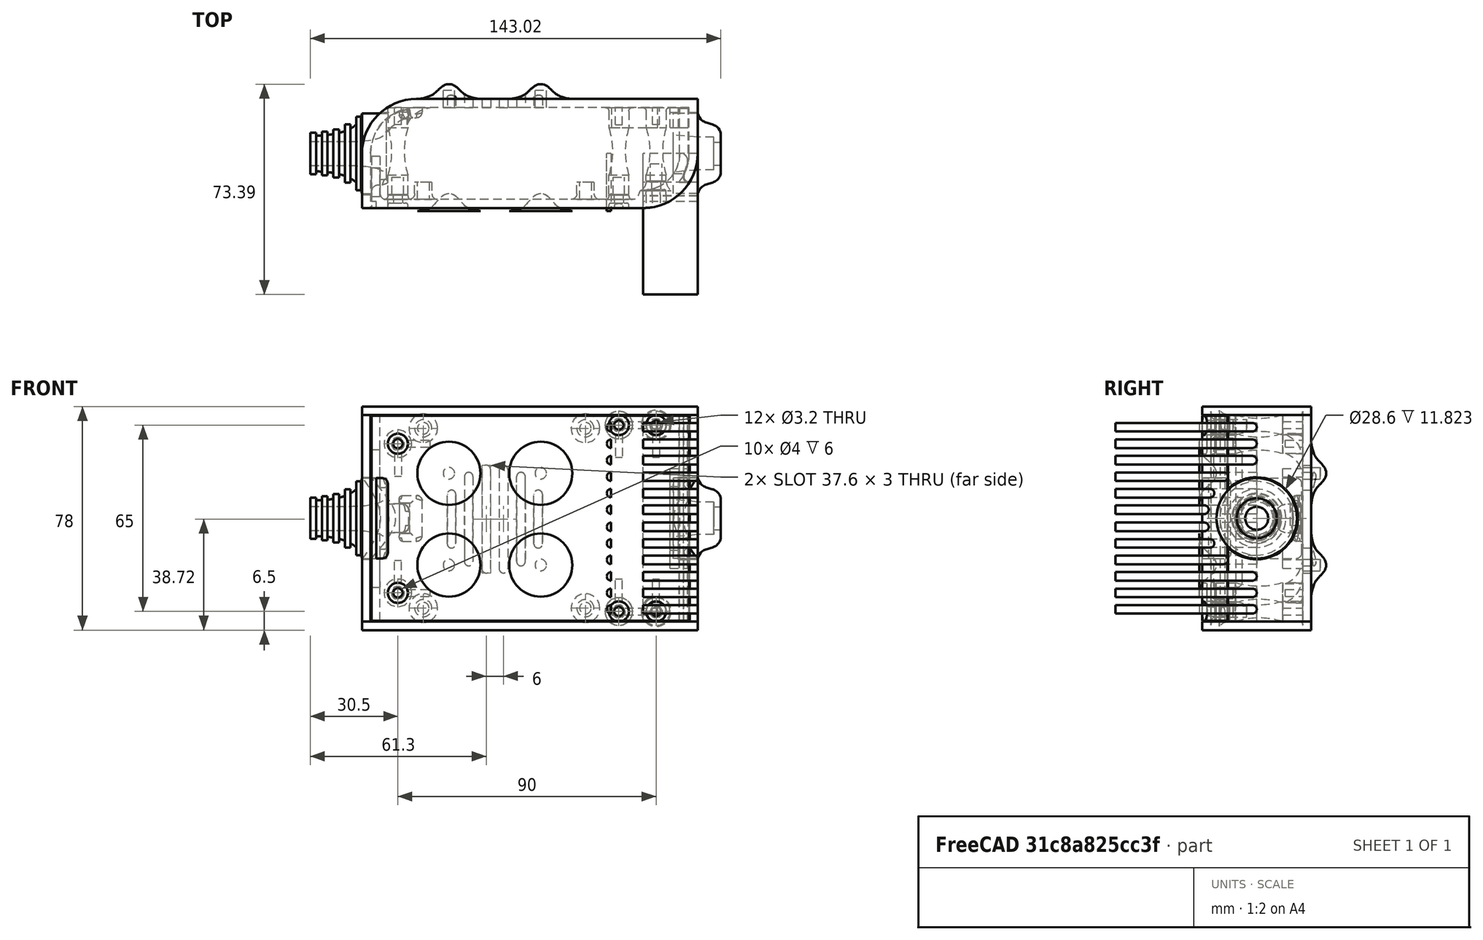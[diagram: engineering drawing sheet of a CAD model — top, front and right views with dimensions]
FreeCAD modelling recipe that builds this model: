
FCSTD DOCUMENT  (FreeCAD 0.19R0.19.2)
Label: enclosure_112
License: All rights reserved
LicenseURL: http://en.wikipedia.org/wiki/All_rights_reserved
objects: Part::Feature×72, Part::Revolution×72, Part::MultiFuse×53, Sketcher::SketchObject×31, Part::Fillet×22, Part::Cylinder×22, Part::Extrusion×21, Part::Cut×20, Part::Box×12, App::MeasureDistance×4
note: 325 computed .brp shape members not serialized (recipe doc carries the construction recipe); baked Part::Feature solids carry a one-line shape summary decoded from their .brp

FEATURE [Sketcher::SketchObject] Sketch  label="topSketch"
  FullyConstrained = true
  sketch-geometry (13):
    g0: LineSegment StartX=117 StartY=19 StartZ=0 EndX=117 EndY=38 EndZ=0
    g1: ArcOfCircle CenterX=98 CenterY=19 CenterZ=0 NormalX=0 NormalY=0 NormalZ=1 AngleXU=0 Radius=19 StartAngle=5.7297 EndAngle=6.28319
    g2: LineSegment StartX=0 StartY=3 StartZ=0 EndX=0 EndY=19 EndZ=0
    g3: LineSegment StartX=19 StartY=38 StartZ=0 EndX=117 EndY=38 EndZ=0
    g4: ArcOfCircle CenterX=19 CenterY=19 CenterZ=0 NormalX=0 NormalY=0 NormalZ=1 AngleXU=0 Radius=19 StartAngle=1.5708 EndAngle=3.14159
    g5: ArcOfCircle CenterX=19 CenterY=19 CenterZ=0 NormalX=0 NormalY=0 NormalZ=1 AngleXU=0 Radius=16 StartAngle=1.5708 EndAngle=3.14159
    g6: ArcOfCircle CenterX=98 CenterY=19 CenterZ=0 NormalX=0 NormalY=0 NormalZ=1 AngleXU=0 Radius=16 StartAngle=5.60905 EndAngle=6.28319
    g7: LineSegment StartX=114 StartY=19 StartZ=0 EndX=114 EndY=35 EndZ=0
    g8: LineSegment StartX=110.5 StartY=9.01251 StartZ=0 EndX=114.163 EndY=9.01251 EndZ=0
    g9: LineSegment StartX=114 StartY=35 StartZ=0 EndX=19 EndY=35 EndZ=0
    g10: LineSegment StartX=0 StartY=3 StartZ=0 EndX=0 EndY=0 EndZ=0
    g11: LineSegment StartX=3 StartY=0 StartZ=0 EndX=0 EndY=0 EndZ=0
    g12: LineSegment StartX=3 StartY=19 StartZ=0 EndX=3 EndY=0 EndZ=0
  constraints (33):
    c: Vertical(g0)
    c: Distance(g0) = 19
    c: Block(g0)
    c: Coincident(g1,g0)
    c: Block(g1)
    c: Vertical(g2)
    c: Block(g2)
    c: Coincident(g3,g0)
    c: Horizontal(g3)
    c: Distance(g3) = 98
    c: Coincident(g4,g3)
    c: Coincident(g4,g2)
    c: Block(g4)
    c: Coincident(g5,g4)
    c: Coincident(g6,g1)
    c: Block(g6)
    c: Block(g5)
    c: Coincident(g7,g6)
    c: Vertical(g7)
    c: Coincident(g8,g6)
    c: Coincident(g8,g1)
    c: Coincident(g9,g7)
    c: Coincident(g9,g5)
    c: Horizontal(g9)
    c: Tangent(g9,g5)
    c: Coincident(g10,g2)
    c: Distance(g10) = 3
    c: Vertical(g10)
    c: Coincident(g11,g10)
    c: Horizontal(g11)
    c: Coincident(g12,g5)
    c: Coincident(g12,g11)
    c: Vertical(g12)
FEATURE [Sketcher::SketchObject] Sketch001  label="bottomSketch"
  FullyConstrained = true
  sketch-geometry (32):
    g0: LineSegment StartX=3.3 StartY=-6.03275e-07 StartZ=0 EndX=98 EndY=-6.03275e-07 EndZ=0
    g1: ArcOfCircle CenterX=98 CenterY=19 CenterZ=0 NormalX=0 NormalY=0 NormalZ=1 AngleXU=0 Radius=19 StartAngle=4.71239 EndAngle=5.71103
    g2: LineSegment StartX=6.3 StartY=8 StartZ=0 EndX=3.3 EndY=8 EndZ=0
    g3: LineSegment StartX=3.3 StartY=8 StartZ=0 EndX=3.3 EndY=-6.03275e-07 EndZ=0
    g4: ArcOfCircle CenterX=8.3 CenterY=5 CenterZ=0 NormalX=0 NormalY=0 NormalZ=1 AngleXU=0 Radius=2 StartAngle=3.14159 EndAngle=4.71239
    g5: LineSegment StartX=6.3 StartY=8 StartZ=0 EndX=6.3 EndY=5 EndZ=0
    g6: ArcOfCircle CenterX=98 CenterY=19 CenterZ=0 NormalX=0 NormalY=0 NormalZ=1 AngleXU=0 Radius=12.7 StartAngle=4.71239 EndAngle=6.28319
    g7: LineSegment StartX=94.7 StartY=3 StartZ=0 EndX=8.3 EndY=3 EndZ=0
    g8-g12: Circle x5 (B-spline internal-alignment scaffolding for g13; pole/knot coordinates omitted)
    g13: BSplineCurve PolesCount=5 KnotsCount=3 Degree=3 IsPeriodic=0
    g14: GeomPoint X=98 Y=6.3 Z=0
    g15: GeomPoint X=96.3938 Y=4.71946 Z=0
    g16: GeomPoint X=94.7 Y=3 Z=0
    g17-g23: Circle x7 (B-spline internal-alignment scaffolding for g24; pole/knot coordinates omitted)
    g24: BSplineCurve PolesCount=7 KnotsCount=5 Degree=3 IsPeriodic=0
    g25-g29: GeomPoint x5 (B-spline internal-alignment scaffolding for g24; pole/knot coordinates omitted)
    g30: ArcOfCircle CenterX=98 CenterY=19 CenterZ=0 NormalX=0 NormalY=0 NormalZ=1 AngleXU=0 Radius=15.7 StartAngle=5.81226 EndAngle=6.28319
    g31: LineSegment StartX=110.7 StartY=19 StartZ=0 EndX=113.7 EndY=19 EndZ=0
  constraints (41):
    c: Horizontal(g0)
    c: Coincident(g1,g0)
    c: Block(g1)
    c: Horizontal(g2)
    c: Distance(g2) = 3
    c: Coincident(g3,g2)
    c: Vertical(g3)
    c: Coincident(g3,g0)
    c: Block(g4)
    c: Block(g2)
    c: Coincident(g5,g2)
    c: Coincident(g5,g4)
    c: Vertical(g5)
    c: Coincident(g6,g1)
    c: Block(g6)
    c: Coincident(g7,g4)
    c: Horizontal(g7)
    c: Block(g0)
    c: Block(g7)
    c: Block(g3)
    c: Coincident(g13,g6)
    c: Weight(g8) = 1
    c: Equal(g8, g9-g12) x4
    c: Coincident(g13,g7)
    c: InternalAlignment(g8-g12 -> g13) x5
    c: InternalAlignment(g14,g13)
    c: InternalAlignment(g15,g13)
    c: InternalAlignment(g16,g13)
    c: Block(g13)
    c: Weight(g17) = 1
    c: Equal(g17, g18-g23) x6
    c: Coincident(g24,g1)
    c: InternalAlignment(g17-g23 -> g24) x7
    c: InternalAlignment(g25-g29 -> g24) x5
    c: Block(g24)
    c: Coincident(g30,g24)
    c: Coincident(g31,g6)
    c: Coincident(g31,g30)
    c: Horizontal(g31)
    c: Block(g31)
    c: Block(g30)
FEATURE [Part::Extrusion] Extrude  label="top"
  Base = -> Sketch
  Dir = (0,0,1)
  DirMode = 2
  FaceMakerClass = Part::FaceMakerBullseye
  LengthFwd = 72
  LengthRev = 0
  Solid = true
  Symmetric = false
FEATURE [Part::Extrusion] Extrude001  label="bottom"
  Base = -> Sketch001
  Dir = (0,0,1)
  DirMode = 2
  FaceMakerClass = Part::FaceMakerBullseye
  LengthFwd = 71.4
  LengthRev = 0
  Placement = pos=(0,0,0.3) rot=(0,0,1;0rad)
  Solid = true
  Symmetric = false
FEATURE [Sketcher::SketchObject] Sketch002  label="topSketch001"
  FullyConstrained = true
  sketch-geometry (6):
    g0: LineSegment StartX=19 StartY=38 StartZ=0 EndX=117 EndY=38 EndZ=0
    g1: ArcOfCircle CenterX=19 CenterY=19 CenterZ=0 NormalX=0 NormalY=0 NormalZ=1 AngleXU=0 Radius=19 StartAngle=1.5708 EndAngle=3.14159
    g2: LineSegment StartX=117 StartY=38 StartZ=0 EndX=117 EndY=19 EndZ=0
    g3: LineSegment StartX=98 StartY=1.0161e-12 StartZ=0 EndX=5.22862e-06 EndY=1.0161e-12 EndZ=0
    g4: LineSegment StartX=5.22862e-06 StartY=19 StartZ=0 EndX=5.22862e-06 EndY=1.0161e-12 EndZ=0
    g5: ArcOfCircle CenterX=98 CenterY=19 CenterZ=0 NormalX=0 NormalY=0 NormalZ=1 AngleXU=0 Radius=19 StartAngle=4.71239 EndAngle=6.28319
  constraints (16):
    c: Horizontal(g0)
    c: Distance(g0) = 98
    c: Coincident(g1,g0)
    c: Block(g1)
    c: Coincident(g2,g0)
    c: Vertical(g2)
    c: Distance(g2) = 19
    c: Horizontal(g3)
    c: Coincident(g4,g1)
    c: Vertical(g4)
    c: Coincident(g3,g4)
    c: Block(g3)
    c: Coincident(g5,g2)
    c: Coincident(g5,g3)
    c: Block(g0)
    c: Block(g5)
FEATURE [Part::Extrusion] Extrude002  label="sideA"
  Base = -> Sketch002
  Dir = (0,0,1)
  DirMode = 2
  FaceMakerClass = Part::FaceMakerBullseye
  LengthFwd = 3
  LengthRev = 0
  Placement = pos=(0,0,-3) rot=(0,0,1;0rad)
  Solid = true
  Symmetric = false
FEATURE [Sketcher::SketchObject] Sketch003  label="topSketch002"
  FullyConstrained = true
  sketch-geometry (6):
    g0: LineSegment StartX=19 StartY=38 StartZ=0 EndX=117 EndY=38 EndZ=0
    g1: ArcOfCircle CenterX=19 CenterY=19 CenterZ=0 NormalX=0 NormalY=0 NormalZ=1 AngleXU=0 Radius=19 StartAngle=1.5708 EndAngle=3.14159
    g2: LineSegment StartX=117 StartY=38 StartZ=0 EndX=117 EndY=19 EndZ=0
    g3: LineSegment StartX=98 StartY=1.0161e-12 StartZ=0 EndX=5.22862e-06 EndY=1.0161e-12 EndZ=0
    g4: LineSegment StartX=5.22862e-06 StartY=19 StartZ=0 EndX=5.22862e-06 EndY=1.0161e-12 EndZ=0
    g5: ArcOfCircle CenterX=98 CenterY=19 CenterZ=0 NormalX=0 NormalY=0 NormalZ=1 AngleXU=0 Radius=19 StartAngle=4.71239 EndAngle=6.28319
  constraints (16):
    c: Horizontal(g0)
    c: Distance(g0) = 98
    c: Coincident(g1,g0)
    c: Block(g1)
    c: Coincident(g2,g0)
    c: Vertical(g2)
    c: Distance(g2) = 19
    c: Horizontal(g3)
    c: Coincident(g4,g1)
    c: Vertical(g4)
    c: Coincident(g3,g4)
    c: Block(g3)
    c: Coincident(g5,g2)
    c: Coincident(g5,g3)
    c: Block(g0)
    c: Block(g5)
FEATURE [Part::Extrusion] Extrude003  label="sideB"
  Base = -> Sketch003
  Dir = (0,0,1)
  DirMode = 2
  FaceMakerClass = Part::FaceMakerBullseye
  LengthFwd = 3
  LengthRev = 0
  Placement = pos=(0,0,72) rot=(0,0,1;0rad)
  Solid = true
  Symmetric = false
FEATURE [Sketcher::SketchObject] Sketch004
  FullyConstrained = true
  MapMode = 3
  Placement = pos=(0,0,0) rot=(1,0,0;1.5708rad)
  Support = -> [Extrude]
  sketch-geometry (8):
    g0: Circle CenterX=80.351 CenterY=-67.6202 CenterZ=0 NormalX=0 NormalY=0 NormalZ=1 AngleXU=0 Radius=2
    g1: Circle CenterX=80.351 CenterY=-67.6202 CenterZ=0 NormalX=0 NormalY=0 NormalZ=1 AngleXU=0 Radius=3
    g2: Circle CenterX=80.351 CenterY=-4.92017 CenterZ=0 NormalX=0 NormalY=0 NormalZ=1 AngleXU=0 Radius=2
    g3: Circle CenterX=80.351 CenterY=-4.92017 CenterZ=0 NormalX=0 NormalY=0 NormalZ=1 AngleXU=0 Radius=3
    g4: Circle CenterX=23.851 CenterY=-4.92017 CenterZ=0 NormalX=0 NormalY=0 NormalZ=1 AngleXU=0 Radius=2
    g5: Circle CenterX=23.851 CenterY=-4.92017 CenterZ=0 NormalX=0 NormalY=0 NormalZ=1 AngleXU=0 Radius=3
    g6: Circle CenterX=23.851 CenterY=-67.6202 CenterZ=0 NormalX=0 NormalY=0 NormalZ=1 AngleXU=0 Radius=2
    g7: Circle CenterX=23.851 CenterY=-67.6202 CenterZ=0 NormalX=0 NormalY=0 NormalZ=1 AngleXU=0 Radius=3
  constraints (8):
    c: Block(g3)
    c: Block(g2)
    c: Block(g1)
    c: Block(g0)
    c: Block(g6)
    c: Block(g7)
    c: Block(g4)
    c: Block(g5)
FEATURE [Part::Extrusion] Extrude004
  Base = -> Sketch004
  Dir = (0,-1,2e-16)
  DirMode = 2
  FaceMakerClass = Part::FaceMakerBullseye
  LengthFwd = 6
  LengthRev = 0
  Placement = pos=(0,9,0) rot=(0,0,1;0rad)
  Solid = true
  Symmetric = false
FEATURE [Sketcher::SketchObject] Sketch005
  FullyConstrained = true
  MapMode = 3
  Placement = pos=(0,0,0) rot=(1,0,0;1.5708rad)
  Support = -> [Extrude]
  sketch-geometry (8):
    g0: Circle CenterX=80.351 CenterY=-67.6202 CenterZ=0 NormalX=0 NormalY=0 NormalZ=1 AngleXU=0 Radius=3
    g1: Circle CenterX=80.351 CenterY=-4.92017 CenterZ=0 NormalX=0 NormalY=0 NormalZ=1 AngleXU=0 Radius=3
    g2: Circle CenterX=23.851 CenterY=-4.92017 CenterZ=0 NormalX=0 NormalY=0 NormalZ=1 AngleXU=0 Radius=3
    g3: Circle CenterX=23.851 CenterY=-67.6202 CenterZ=0 NormalX=0 NormalY=0 NormalZ=1 AngleXU=0 Radius=3
    g4: Circle CenterX=23.851 CenterY=-67.6202 CenterZ=0 NormalX=0 NormalY=0 NormalZ=1 AngleXU=0 Radius=5
    g5: Circle CenterX=80.351 CenterY=-67.6202 CenterZ=0 NormalX=0 NormalY=0 NormalZ=1 AngleXU=0 Radius=5
    g6: Circle CenterX=23.851 CenterY=-4.92017 CenterZ=0 NormalX=0 NormalY=0 NormalZ=1 AngleXU=0 Radius=5
    g7: Circle CenterX=80.351 CenterY=-4.92017 CenterZ=0 NormalX=0 NormalY=0 NormalZ=1 AngleXU=0 Radius=5
  constraints (8):
    c: Block(g1)
    c: Block(g0)
    c: Block(g3)
    c: Block(g2)
    c: Block(g5)
    c: Block(g4)
    c: Block(g6)
    c: Block(g7)
FEATURE [Part::Extrusion] Extrude005
  Base = -> Sketch005
  Dir = (0,-1,2e-16)
  DirMode = 2
  FaceMakerClass = Part::FaceMakerBullseye
  LengthFwd = 2
  LengthRev = 0
  Solid = true
  Symmetric = false
FEATURE [Sketcher::SketchObject] Sketch006
  FullyConstrained = true
  MapMode = 3
  Placement = pos=(0,0,0) rot=(1,0,0;1.5708rad)
  sketch-geometry (8):
    g0: Circle CenterX=80.351 CenterY=-67.6202 CenterZ=0 NormalX=0 NormalY=0 NormalZ=1 AngleXU=0 Radius=3
    g1: Circle CenterX=80.351 CenterY=-4.92017 CenterZ=0 NormalX=0 NormalY=0 NormalZ=1 AngleXU=0 Radius=3
    g2: Circle CenterX=23.851 CenterY=-4.92017 CenterZ=0 NormalX=0 NormalY=0 NormalZ=1 AngleXU=0 Radius=3
    g3: Circle CenterX=23.851 CenterY=-67.6202 CenterZ=0 NormalX=0 NormalY=0 NormalZ=1 AngleXU=0 Radius=3
    g4: Circle CenterX=23.851 CenterY=-67.6202 CenterZ=0 NormalX=0 NormalY=0 NormalZ=1 AngleXU=0 Radius=5
    g5: Circle CenterX=80.351 CenterY=-67.6202 CenterZ=0 NormalX=0 NormalY=0 NormalZ=1 AngleXU=0 Radius=5
    g6: Circle CenterX=23.851 CenterY=-4.92017 CenterZ=0 NormalX=0 NormalY=0 NormalZ=1 AngleXU=0 Radius=5
    g7: Circle CenterX=80.351 CenterY=-4.92017 CenterZ=0 NormalX=0 NormalY=0 NormalZ=1 AngleXU=0 Radius=5
  constraints (8):
    c: Block(g1)
    c: Block(g0)
    c: Block(g3)
    c: Block(g2)
    c: Block(g5)
    c: Block(g4)
    c: Block(g6)
    c: Block(g7)
FEATURE [Part::Extrusion] Extrude007
  Base = -> Sketch006
  Dir = (0,-1,2e-16)
  DirMode = 2
  FaceMakerClass = Part::FaceMakerBullseye
  LengthFwd = 2
  LengthRev = 0
  Solid = true
  Symmetric = false
FEATURE [Part::Fillet] Fillet
  Base = -> Extrude007
  Edges = 4 edges r=1.99: [Edge6,Edge12,Edge18,Edge24]
FEATURE [Part::Cut] Cut
  Base = -> Extrude005
  Placement = pos=(0,5,0) rot=(0,0,1;0rad)
  Tool = -> Fillet
FEATURE [Part::MultiFuse] Fusion  label="pCBScrews"
  Placement = pos=(-2.5,0,72.3) rot=(0,0,1;0rad)
  Shapes = -> [Extrude004,Cut]
FEATURE [App::MeasureDistance] Distance  label="Distance: 0.69 mm"
  Distance = 0.685967
  P1 = (24.0138,2.9647,0.3)
  P2 = (23.8901,3,-0.373787)
FEATURE [App::MeasureDistance] Distance001  label="Distance: 0.53 mm"
  Distance = 0.533607
  P1 = (80.2939,3,72.2334)
  P2 = (80.281,2.99661,71.7)
FEATURE [Part::Fillet] Fillet001
  Base = -> Extrude001
  Edges = 1 edges r=2.4: [Edge17]
FEATURE [Part::Fillet] Fillet002  label="bottom001"
  Base = -> Fillet001
  Edges = 1 edges r=2.4: [Edge36]
FEATURE [Part::Fillet] Fillet003  label="top001"
  Base = -> Extrude
  Edges = 1 edges r=2: [Edge1]
FEATURE [Sketcher::SketchObject] Sketch007
  FullyConstrained = true
  sketch-geometry (16):
    g0: LineSegment StartX=4 StartY=0 StartZ=0 EndX=4 EndY=2.4 EndZ=0
    g1: LineSegment StartX=4 StartY=2.4 StartZ=0 EndX=7 EndY=2.4 EndZ=0
    g2: LineSegment StartX=4 StartY=0 StartZ=0 EndX=5.7 EndY=0 EndZ=0
    g3: LineSegment StartX=5.7 StartY=0 StartZ=0 EndX=5.7 EndY=-5.6 EndZ=0
    g4-g8: Circle x5 (B-spline internal-alignment scaffolding for g9; pole/knot coordinates omitted)
    g9: BSplineCurve PolesCount=5 KnotsCount=3 Degree=3 IsPeriodic=0
    g10: GeomPoint X=7 Y=2.4 Z=0
    g11: GeomPoint X=10.4582 Y=-1.55472 Z=0
    g12: GeomPoint X=14 Y=-5.6 Z=0
    g13: LineSegment StartX=14 StartY=-5.6 StartZ=0 EndX=14 EndY=-14.1 EndZ=0
    g14: LineSegment StartX=14 StartY=-14.1 StartZ=0 EndX=6.5 EndY=-14.1 EndZ=0
    g15: LineSegment StartX=5.7 StartY=-5.6 StartZ=0 EndX=6.5 EndY=-14.1 EndZ=0
  constraints (28):
    c: Distance(g0) = 2.4
    c: Vertical(g0)
    c: Block(g0)
    c: Coincident(g1,g0)
    c: Horizontal(g1)
    c: Distance(g1) = 3
    c: Coincident(g2,g0)
    c: Horizontal(g2)
    c: Distance(g2) = 1.7
    c: Coincident(g3,g2)
    c: Vertical(g3)
    c: Distance(g3) = 5.6
    c: Coincident(g9,g1)
    c: Weight(g4) = 1
    c: Equal(g4, g5-g8) x4
    c: InternalAlignment(g4-g8 -> g9) x5
    c: InternalAlignment(g10,g9)
    c: InternalAlignment(g11,g9)
    c: InternalAlignment(g12,g9)
    c: Block(g9)
    c: Coincident(g13,g9)
    c: Vertical(g13)
    c: Distance(g13) = 8.5
    c: Coincident(g14,g13)
    c: Horizontal(g14)
    c: Distance(g14) = 7.5
    c: Coincident(g15,g3)
    c: Coincident(g15,g14)
FEATURE [Part::Feature] Face
  shape: bbox 10 x 16.5 x 2e-07 mm, 1 faces, 0 solids (baked)
FEATURE [Part::Revolution] Revolve  label="plugHousing"
  Angle = 360
  Axis = (0,1,0)
  Base = (0,0,0)
  FaceMakerClass = Part::FaceMakerBullseye
  Placement = pos=(0,0,36.15) rot=(0,0,1;0rad)
  Solid = false
  Source = -> Face
  Symmetric = false
FEATURE [Part::Feature] Face001
  shape: bbox 10 x 16.5 x 2e-07 mm, 1 faces, 0 solids (baked)
FEATURE [Part::Revolution] Revolve001  label="plugHousing001"
  Angle = 360
  Axis = (0,1,0)
  Base = (0,0,0)
  FaceMakerClass = Part::FaceMakerBullseye
  Placement = pos=(0,0,36.15) rot=(0,0,1;0rad)
  Solid = false
  Source = -> Face001
  Symmetric = false
FEATURE [Part::MultiFuse] Fusion001  label="plugHousing002"
  Placement = pos=(0,0,0) rot=(0,0,1;1.5708rad)
  Shapes = -> [Revolve001,Revolve]
FEATURE [Part::Feature] Face002
  shape: bbox 10 x 16.5 x 2e-07 mm, 1 faces, 0 solids (baked)
FEATURE [Part::Revolution] Revolve003  label="plugHousing005"
  Angle = 360
  Axis = (0,1,0)
  Base = (0,0,0)
  FaceMakerClass = Part::FaceMakerBullseye
  Placement = pos=(0,0,36.15) rot=(0,0,1;0rad)
  Solid = false
  Source = -> Face002
  Symmetric = false
FEATURE [Part::Feature] Face003
  shape: bbox 10 x 16.5 x 2e-07 mm, 1 faces, 0 solids (baked)
FEATURE [Part::Revolution] Revolve002  label="plugHousing003"
  Angle = 360
  Axis = (0,1,0)
  Base = (0,0,0)
  FaceMakerClass = Part::FaceMakerBullseye
  Placement = pos=(0,0,36.15) rot=(0,0,1;0rad)
  Solid = false
  Source = -> Face003
  Symmetric = false
FEATURE [Part::MultiFuse] Fusion002  label="plugHousing004"
  Placement = pos=(0,0,0) rot=(0,0,1;1.5708rad)
  Shapes = -> [Revolve002,Revolve003]
FEATURE [Part::MultiFuse] Fusion003  label="plugHousing006"
  Placement = pos=(0,19,0) rot=(0,0,1;3.14159rad)
  Shapes = -> [Fusion002,Fusion001]
FEATURE [Part::Feature] Face004
  shape: bbox 10 x 16.5 x 2e-07 mm, 1 faces, 0 solids (baked)
FEATURE [Part::Revolution] Revolve006  label="plugHousing010"
  Angle = 360
  Axis = (0,1,0)
  Base = (0,0,0)
  FaceMakerClass = Part::FaceMakerBullseye
  Placement = pos=(0,0,36.15) rot=(0,0,1;0rad)
  Solid = false
  Source = -> Face004
  Symmetric = false
FEATURE [Part::Feature] Face005
  shape: bbox 10 x 16.5 x 2e-07 mm, 1 faces, 0 solids (baked)
FEATURE [Part::Revolution] Revolve007  label="plugHousing011"
  Angle = 360
  Axis = (0,1,0)
  Base = (0,0,0)
  FaceMakerClass = Part::FaceMakerBullseye
  Placement = pos=(0,0,36.15) rot=(0,0,1;0rad)
  Solid = false
  Source = -> Face005
  Symmetric = false
FEATURE [Part::Feature] Face006
  shape: bbox 10 x 16.5 x 2e-07 mm, 1 faces, 0 solids (baked)
FEATURE [Part::Revolution] Revolve004  label="plugHousing007"
  Angle = 360
  Axis = (0,1,0)
  Base = (0,0,0)
  FaceMakerClass = Part::FaceMakerBullseye
  Placement = pos=(0,0,36.15) rot=(0,0,1;0rad)
  Solid = false
  Source = -> Face006
  Symmetric = false
FEATURE [Part::MultiFuse] Fusion004  label="plugHousing009"
  Placement = pos=(0,0,0) rot=(0,0,1;1.5708rad)
  Shapes = -> [Revolve004,Revolve007]
FEATURE [Part::Feature] Face007
  shape: bbox 10 x 16.5 x 2e-07 mm, 1 faces, 0 solids (baked)
FEATURE [Part::Revolution] Revolve005  label="plugHousing008"
  Angle = 360
  Axis = (0,1,0)
  Base = (0,0,0)
  FaceMakerClass = Part::FaceMakerBullseye
  Placement = pos=(0,0,36.15) rot=(0,0,1;0rad)
  Solid = false
  Source = -> Face007
  Symmetric = false
FEATURE [Part::MultiFuse] Fusion005  label="plugHousing012"
  Placement = pos=(0,0,0) rot=(0,0,1;1.5708rad)
  Shapes = -> [Revolve006,Revolve005]
FEATURE [Part::MultiFuse] Fusion006  label="plugHousing013"
  Placement = pos=(0,19,0) rot=(0,0,1;3.14159rad)
  Shapes = -> [Fusion005,Fusion004]
FEATURE [Part::MultiFuse] Fusion007  label="plugHousing014"
  Placement = pos=(122.621,0,-0.15) rot=(0,0,1;0rad)
  Shapes = -> [Fusion003,Fusion006]
FEATURE [Part::Cylinder] Cylinder002
  Angle = 360
  AttacherType = Attacher::AttachEngine3D
  Height = 20
  Placement = pos=(0,0,36.15) rot=(0,0,1;0rad)
  Radius = 4
FEATURE [Part::Cylinder] Cylinder003
  Angle = 360
  AttacherType = Attacher::AttachEngine3D
  Height = 10
  Placement = pos=(0,0,36.15) rot=(0,0,1;0rad)
  Radius = 4
FEATURE [Part::MultiFuse] Fusion009  label="removeToCreateHoleForPlugHousing"
  Placement = pos=(70,19,36.15) rot=(0,1,0;1.5708rad)
  Shapes = -> [Cylinder002,Cylinder003]
FEATURE [Part::Cylinder] Cylinder004
  Angle = 360
  AttacherType = Attacher::AttachEngine3D
  Height = 20
  Placement = pos=(0,0,36.15) rot=(0,0,1;0rad)
  Radius = 4
FEATURE [Part::Cylinder] Cylinder005
  Angle = 360
  AttacherType = Attacher::AttachEngine3D
  Height = 10
  Placement = pos=(0,0,36.15) rot=(0,0,1;0rad)
  Radius = 4
FEATURE [Part::MultiFuse] Fusion010  label="removeToCreateHoleForPlugHousing001"
  Placement = pos=(70,19,36.15) rot=(0,1,0;1.5708rad)
  Shapes = -> [Cylinder004,Cylinder005]
FEATURE [Part::Cut] Cut001
  Base = -> Fillet003
  Tool = -> Fusion010
FEATURE [Part::Cut] Cut002  label="Bottom"
  Base = -> Fillet002
  Tool = -> Fusion009
FEATURE [Part::Feature] Face008
  shape: bbox 10 x 16.5 x 2e-07 mm, 1 faces, 0 solids (baked)
FEATURE [Part::Revolution] Revolve011  label="plugHousing021"
  Angle = 360
  Axis = (0,1,0)
  Base = (0,0,0)
  FaceMakerClass = Part::FaceMakerBullseye
  Placement = pos=(0,0,36.15) rot=(0,0,1;0rad)
  Solid = false
  Source = -> Face008
  Symmetric = false
FEATURE [Part::Feature] Face009
  shape: bbox 10 x 16.5 x 2e-07 mm, 1 faces, 0 solids (baked)
FEATURE [Part::Revolution] Revolve012  label="plugHousing022"
  Angle = 360
  Axis = (0,1,0)
  Base = (0,0,0)
  FaceMakerClass = Part::FaceMakerBullseye
  Placement = pos=(0,0,36.15) rot=(0,0,1;0rad)
  Solid = false
  Source = -> Face009
  Symmetric = false
FEATURE [Part::Feature] Face010 .. Face013  x4 (patterned run collapsed; names and placements below)
  shape: bbox 10 x 16.5 x 2e-07 mm, 1 faces, 0 solids (baked)
FEATURE [Part::Revolution] Revolve015  label="plugHousing027"
  Angle = 360
  Axis = (0,1,0)
  Base = (0,0,0)
  FaceMakerClass = Part::FaceMakerBullseye
  Placement = pos=(0,0,36.15) rot=(0,0,1;0rad)
  Solid = false
  Source = -> Face013
  Symmetric = false
FEATURE [Part::Feature] Face014
  shape: bbox 10 x 16.5 x 2e-07 mm, 1 faces, 0 solids (baked)
FEATURE [Part::Feature] Face015
  shape: bbox 10 x 16.5 x 2e-07 mm, 1 faces, 0 solids (baked)
FEATURE [Part::Feature] Face016
  shape: bbox 10 x 16.5 x 2e-07 mm, 1 faces, 0 solids (baked)
FEATURE [Part::Revolution] Revolve019  label="plugHousing033"
  Angle = 360
  Axis = (0,1,0)
  Base = (0,0,0)
  FaceMakerClass = Part::FaceMakerBullseye
  Placement = pos=(0,0,36.15) rot=(0,0,1;0rad)
  Solid = false
  Source = -> Face016
  Symmetric = false
FEATURE [Part::Feature] Face017
  shape: bbox 10 x 16.5 x 2e-07 mm, 1 faces, 0 solids (baked)
FEATURE [Part::Revolution] Revolve020  label="plugHousing034"
  Angle = 360
  Axis = (0,1,0)
  Base = (0,0,0)
  FaceMakerClass = Part::FaceMakerBullseye
  Placement = pos=(0,0,36.15) rot=(0,0,1;0rad)
  Solid = false
  Source = -> Face017
  Symmetric = false
FEATURE [Part::Feature] Face018
  shape: bbox 10 x 16.5 x 2e-07 mm, 1 faces, 0 solids (baked)
FEATURE [Part::Revolution] Revolve016  label="plugHousing030"
  Angle = 360
  Axis = (0,1,0)
  Base = (0,0,0)
  FaceMakerClass = Part::FaceMakerBullseye
  Placement = pos=(0,0,36.15) rot=(0,0,1;0rad)
  Solid = false
  Source = -> Face018
  Symmetric = false
FEATURE [Part::MultiFuse] Fusion020  label="plugHousing038"
  Placement = pos=(0,0,0) rot=(0,0,1;1.5708rad)
  Shapes = -> [Revolve016,Revolve020]
FEATURE [Part::Feature] Face019
  shape: bbox 10 x 16.5 x 2e-07 mm, 1 faces, 0 solids (baked)
FEATURE [Part::Feature] Face020
  shape: bbox 10 x 16.5 x 2e-07 mm, 1 faces, 0 solids (baked)
FEATURE [Part::Revolution] Revolve017  label="plugHousing031"
  Angle = 360
  Axis = (0,1,0)
  Base = (0,0,0)
  FaceMakerClass = Part::FaceMakerBullseye
  Placement = pos=(0,0,36.15) rot=(0,0,1;0rad)
  Solid = false
  Source = -> Face020
  Symmetric = false
FEATURE [Part::MultiFuse] Fusion021  label="plugHousing039"
  Placement = pos=(0,0,0) rot=(0,0,1;1.5708rad)
  Shapes = -> [Revolve019,Revolve017]
FEATURE [Part::MultiFuse] Fusion023  label="plugHousing041"
  Placement = pos=(0,19,0) rot=(0,0,1;3.14159rad)
  Shapes = -> [Fusion021,Fusion020]
FEATURE [Part::Revolution] Revolve022  label="plugHousing043"
  Angle = 360
  Axis = (0,1,0)
  Base = (0,0,0)
  FaceMakerClass = Part::FaceMakerBullseye
  Placement = pos=(0,0,36.15) rot=(0,0,1;0rad)
  Solid = false
  Source = -> Face019
  Symmetric = false
FEATURE [Part::Feature] Face021
  shape: bbox 10 x 16.5 x 2e-07 mm, 1 faces, 0 solids (baked)
FEATURE [Part::Revolution] Revolve023  label="plugHousing044"
  Angle = 360
  Axis = (0,1,0)
  Base = (0,0,0)
  FaceMakerClass = Part::FaceMakerBullseye
  Placement = pos=(0,0,36.15) rot=(0,0,1;0rad)
  Solid = false
  Source = -> Face021
  Symmetric = false
FEATURE [Part::Feature] Face022
  shape: bbox 10 x 16.5 x 2e-07 mm, 1 faces, 0 solids (baked)
FEATURE [Part::Revolution] Revolve018  label="plugHousing032"
  Angle = 360
  Axis = (0,1,0)
  Base = (0,0,0)
  FaceMakerClass = Part::FaceMakerBullseye
  Placement = pos=(0,0,36.15) rot=(0,0,1;0rad)
  Solid = false
  Source = -> Face022
  Symmetric = false
FEATURE [Part::MultiFuse] Fusion022  label="plugHousing040"
  Placement = pos=(0,0,0) rot=(0,0,1;1.5708rad)
  Shapes = -> [Revolve018,Revolve023]
FEATURE [Part::Feature] Face023
  shape: bbox 10 x 16.5 x 2e-07 mm, 1 faces, 0 solids (baked)
FEATURE [Part::Revolution] Revolve021  label="plugHousing035"
  Angle = 360
  Axis = (0,1,0)
  Base = (0,0,0)
  FaceMakerClass = Part::FaceMakerBullseye
  Placement = pos=(0,0,36.15) rot=(0,0,1;0rad)
  Solid = false
  Source = -> Face023
  Symmetric = false
FEATURE [Part::MultiFuse] Fusion018  label="plugHousing036"
  Placement = pos=(0,0,0) rot=(0,0,1;1.5708rad)
  Shapes = -> [Revolve022,Revolve021]
FEATURE [Part::MultiFuse] Fusion019  label="plugHousing037"
  Placement = pos=(0,19,0) rot=(0,0,1;3.14159rad)
  Shapes = -> [Fusion018,Fusion022]
FEATURE [Part::MultiFuse] Fusion024  label="plugHousing042"
  Placement = pos=(122.621,0,-0.15) rot=(0,0,1;0rad)
  Shapes = -> [Fusion023,Fusion019]
FEATURE [Part::Cylinder] Cylinder006
  Angle = 360
  AttacherType = Attacher::AttachEngine3D
  Height = 20
  Placement = pos=(0,0,36.15) rot=(0,0,1;0rad)
  Radius = 14.3
FEATURE [Part::Cylinder] Cylinder007
  Angle = 360
  AttacherType = Attacher::AttachEngine3D
  Height = 10
  Placement = pos=(0,0,36.15) rot=(0,0,1;0rad)
  Radius = 4
FEATURE [Part::MultiFuse] Fusion026  label="removeToCreteHoleForPlugHousing"
  Placement = pos=(70,19,36) rot=(0,1,0;1.5708rad)
  Shapes = -> [Cylinder006,Cylinder007]
FEATURE [Part::Box] Box001  label="Cube001"
  AttacherType = Attacher::AttachEngine3D
  Height = 28
  Length = 3
  Placement = pos=(110.7,19,22) rot=(0,0,1;0rad)
  Width = 15.7
FEATURE [Part::Cut] Cut003  label="top002"
  Base = -> Cut001
  Tool = -> Fusion007
FEATURE [Part::Revolution] Revolve008  label="plugHousing015"
  Angle = 360
  Axis = (0,1,0)
  Base = (0,0,0)
  FaceMakerClass = Part::FaceMakerBullseye
  Placement = pos=(0,0,36.15) rot=(0,0,1;0rad)
  Solid = false
  Source = -> Face010
  Symmetric = false
FEATURE [Part::MultiFuse] Fusion013  label="plugHousing020"
  Placement = pos=(0,0,0) rot=(0,0,1;1.5708rad)
  Shapes = -> [Revolve008,Revolve012]
FEATURE [Part::Cut] Cut004  label="top003"
  Base = -> Cut003
  Placement = pos=(1,0,0) rot=(0,0,1;0rad)
  Tool = -> Fusion026
FEATURE [Part::Cylinder] Cylinder008
  Angle = 360
  AttacherType = Attacher::AttachEngine3D
  Height = 20
  Placement = pos=(0,0,36.15) rot=(0,0,1;0rad)
  Radius = 10.3
FEATURE [Part::Cylinder] Cylinder009
  Angle = 360
  AttacherType = Attacher::AttachEngine3D
  Height = 10
  Placement = pos=(0,0,36.15) rot=(0,0,1;0rad)
  Radius = 4
FEATURE [Part::MultiFuse] Fusion027  label="removeToCreteHoleForPlugHousing001"
  Placement = pos=(70,19,36) rot=(0,1,0;1.5708rad)
  Shapes = -> [Cylinder008,Cylinder009]
FEATURE [Part::Cut] Cut005  label="plugHousingTab"
  Base = -> Box001
  Tool = -> Fusion027
FEATURE [Part::MultiFuse] Fusion028  label="plugHousing045"
  Shapes = -> [Fusion024,Cut005]
FEATURE [Part::Box] Box002  label="Cube002"
  AttacherType = Attacher::AttachEngine3D
  Height = 28.8
  Length = 3
  Placement = pos=(107.3,28,21.6) rot=(0,0,1;0rad)
  Width = 7
FEATURE [Part::Box] Box003  label="Cube003"
  AttacherType = Attacher::AttachEngine3D
  Height = 3
  Length = 6.4
  Placement = pos=(107.3,28,18.6) rot=(0,0,1;0rad)
  Width = 7
FEATURE [Part::Box] Box004  label="Cube004"
  AttacherType = Attacher::AttachEngine3D
  Height = 3
  Length = 6.4
  Placement = pos=(107.3,28,50.4) rot=(0,0,1;0rad)
  Width = 7
FEATURE [Part::MultiFuse] Fusion029  label="plugHousingBracketHolder"
  Shapes = -> [Box004,Box002,Box003]
FEATURE [Part::Cylinder] Cylinder010
  Angle = 360
  AttacherType = Attacher::AttachEngine3D
  Height = 20
  Placement = pos=(0,0,36.15) rot=(0,0,1;0rad)
  Radius = 14.3
FEATURE [Part::Cylinder] Cylinder011
  Angle = 360
  AttacherType = Attacher::AttachEngine3D
  Height = 10
  Placement = pos=(0,0,36.15) rot=(0,0,1;0rad)
  Radius = 4
FEATURE [Part::MultiFuse] Fusion030  label="removeToCreteHoleForPlugHousing002"
  Placement = pos=(70,19,36) rot=(0,1,0;1.5708rad)
  Shapes = -> [Cylinder010,Cylinder011]
FEATURE [Part::Cut] Cut006  label="plugHousingBracketHolder001"
  Base = -> Fusion029
  Tool = -> Fusion030
FEATURE [Part::Cylinder] Cylinder012
  Angle = 360
  AttacherType = Attacher::AttachEngine3D
  Height = 20
  Placement = pos=(0,0,36.15) rot=(0,0,1;0rad)
  Radius = 7
FEATURE [Part::Cylinder] Cylinder013
  Angle = 360
  AttacherType = Attacher::AttachEngine3D
  Height = 10
  Placement = pos=(0,0,36.15) rot=(0,0,1;0rad)
  Radius = 4
FEATURE [Part::MultiFuse] Fusion032  label="removeToCreteHoleForPlugHousing003"
  Placement = pos=(70,19,36) rot=(0,1,0;1.5708rad)
  Shapes = -> [Cylinder012,Cylinder013]
FEATURE [Part::Cut] Cut007  label="bottom002"
  Base = -> Cut002
  Tool = -> Fusion032
FEATURE [Sketcher::SketchObject] Sketch008
  FullyConstrained = true
  sketch-geometry (54):
    g0: LineSegment StartX=-4.2 StartY=0 StartZ=0 EndX=-6.2 EndY=0 EndZ=0
    g1: LineSegment StartX=-14 StartY=-18 StartZ=0 EndX=-14 EndY=-26.5 EndZ=0
    g2: LineSegment StartX=-4.2 StartY=0 StartZ=0 EndX=-4.2 EndY=-13.4877 EndZ=0
    g3: Circle CenterX=-4.2 CenterY=-13.4877 CenterZ=0 NormalX=0 NormalY=0 NormalZ=1 AngleXU=0 Radius=1
    g4: Circle CenterX=-4.2 CenterY=-26.5 CenterZ=0 NormalX=0 NormalY=0 NormalZ=1 AngleXU=0 Radius=1
    g5: Circle CenterX=-8.2 CenterY=-26.5 CenterZ=0 NormalX=0 NormalY=0 NormalZ=1 AngleXU=0 Radius=1
    g6: BSplineCurve PolesCount=3 KnotsCount=2 Degree=2 IsPeriodic=0
    g7: GeomPoint X=-4.2 Y=-13.4877 Z=0
    g8: GeomPoint X=-8.2 Y=-26.5 Z=0
    g9: LineSegment StartX=-14 StartY=-26.5 StartZ=0 EndX=-8.2 EndY=-26.5 EndZ=0
    g10: LineSegment StartX=-10.15 StartY=-12 StartZ=0 EndX=-10.15 EndY=-14 EndZ=0
    g11: LineSegment StartX=-12.8401 StartY=-16 StartZ=0 EndX=-10.1571 EndY=-16 EndZ=0
    g12: LineSegment StartX=-10.15 StartY=-14 StartZ=0 EndX=-8.70761 EndY=-14 EndZ=0
    g13: LineSegment StartX=-12.8401 StartY=-16 StartZ=0 EndX=-12.8401 EndY=-17.6958 EndZ=0
    g14: LineSegment StartX=-10.15 StartY=-12 StartZ=0 EndX=-7.79258 EndY=-12 EndZ=0
    g15: Circle CenterX=-6.2215 CenterY=-2 CenterZ=0 NormalX=0 NormalY=0 NormalZ=1 AngleXU=0 Radius=1
    g16: Circle CenterX=-6.22762 CenterY=-2.58724 CenterZ=0 NormalX=0 NormalY=0 NormalZ=1 AngleXU=0 Radius=1
    g17: Circle CenterX=-6.32538 CenterY=-4 CenterZ=0 NormalX=0 NormalY=0 NormalZ=1 AngleXU=0 Radius=1
    g18: BSplineCurve PolesCount=3 KnotsCount=2 Degree=2 IsPeriodic=0
    g19: GeomPoint X=-6.2215 Y=-2 Z=0
    g20: GeomPoint X=-6.32538 Y=-4 Z=0
    g21: Circle CenterX=-6.48644 CenterY=-5.99526 CenterZ=0 NormalX=0 NormalY=0 NormalZ=1 AngleXU=0 Radius=1
    g22: Circle CenterX=-6.58486 CenterY=-6.99526 CenterZ=0 NormalX=0 NormalY=0 NormalZ=1 AngleXU=0 Radius=1
    g23: Circle CenterX=-6.77343 CenterY=-8 CenterZ=0 NormalX=0 NormalY=0 NormalZ=1 AngleXU=0 Radius=1
    g24: BSplineCurve PolesCount=3 KnotsCount=2 Degree=2 IsPeriodic=0
    g25: GeomPoint X=-6.48644 Y=-5.99526 Z=0
    g26: GeomPoint X=-6.77343 Y=-8 Z=0
    g27: Circle CenterX=-7.19003 CenterY=-10 CenterZ=0 NormalX=0 NormalY=0 NormalZ=1 AngleXU=0 Radius=1
    g28: Circle CenterX=-7.44407 CenterY=-11.0915 CenterZ=0 NormalX=0 NormalY=0 NormalZ=1 AngleXU=0 Radius=1
    g29: Circle CenterX=-7.79258 CenterY=-12 CenterZ=0 NormalX=0 NormalY=0 NormalZ=1 AngleXU=0 Radius=1
    g30: BSplineCurve PolesCount=3 KnotsCount=2 Degree=2 IsPeriodic=0
    g31: GeomPoint X=-7.19003 Y=-10 Z=0
    g32: GeomPoint X=-7.79258 Y=-12 Z=0
    g33: Circle CenterX=-8.70761 CenterY=-14 CenterZ=0 NormalX=0 NormalY=0 NormalZ=1 AngleXU=0 Radius=1
    g34: Circle CenterX=-9.33087 CenterY=-15.1837 CenterZ=0 NormalX=0 NormalY=0 NormalZ=1 AngleXU=0 Radius=1
    g35: Circle CenterX=-10.1571 CenterY=-16 CenterZ=0 NormalX=0 NormalY=0 NormalZ=1 AngleXU=0 Radius=1
    g36: BSplineCurve PolesCount=3 KnotsCount=2 Degree=2 IsPeriodic=0
    g37: GeomPoint X=-8.70761 Y=-14 Z=0
    g38: GeomPoint X=-10.1571 Y=-16 Z=0
    g39: Circle CenterX=-12.8401 CenterY=-17.6958 CenterZ=0 NormalX=0 NormalY=0 NormalZ=1 AngleXU=0 Radius=1
    g40: Circle CenterX=-13.3521 CenterY=-17.9027 CenterZ=0 NormalX=0 NormalY=0 NormalZ=1 AngleXU=0 Radius=1
    g41: Circle CenterX=-14 CenterY=-18 CenterZ=0 NormalX=0 NormalY=0 NormalZ=1 AngleXU=0 Radius=1
    g42: BSplineCurve PolesCount=3 KnotsCount=2 Degree=2 IsPeriodic=0
    g43: GeomPoint X=-12.8401 Y=-17.6958 Z=0
    g44: GeomPoint X=-14 Y=-18 Z=0
    g45: LineSegment StartX=-6.2 StartY=0 StartZ=0 EndX=-7.2 EndY=0 EndZ=0
    g46: LineSegment StartX=-7.2 StartY=0 StartZ=0 EndX=-7.2 EndY=-2 EndZ=0
    g47: LineSegment StartX=-7.2 StartY=-2 StartZ=0 EndX=-6.2215 EndY=-2 EndZ=0
    g48: LineSegment StartX=-6.32538 StartY=-4 StartZ=0 EndX=-7.65538 EndY=-4 EndZ=0
    g49: LineSegment StartX=-7.65538 StartY=-4 StartZ=0 EndX=-7.65538 EndY=-5.99526 EndZ=0
    g50: LineSegment StartX=-7.65538 StartY=-5.99526 StartZ=0 EndX=-6.48644 EndY=-5.99526 EndZ=0
    g51: LineSegment StartX=-6.77343 StartY=-8 StartZ=0 EndX=-8.43343 EndY=-8 EndZ=0
    g52: LineSegment StartX=-8.43343 StartY=-8 StartZ=0 EndX=-8.43343 EndY=-10 EndZ=0
    g53: LineSegment StartX=-8.43343 StartY=-10 StartZ=0 EndX=-7.19003 EndY=-10 EndZ=0
  constraints (112):
    c: Horizontal(g0)
    c: Distance(g0) = 2
    c: Block(g0)
    c: Vertical(g1)
    c: Coincident(g2,g0)
    c: Vertical(g2)
    c: Block(g2)
    c: Coincident(g6,g2)
    c: Weight(g3) = 1
    c: Equal(g3,g4)
    c: Equal(g3,g5)
    c: InternalAlignment(g3,g6)
    c: InternalAlignment(g4,g6)
    c: InternalAlignment(g5,g6)
    c: InternalAlignment(g7,g6)
    c: InternalAlignment(g8,g6)
    c: Block(g6)
    c: Coincident(g9,g1)
    c: Coincident(g9,g6)
    c: Horizontal(g9)
    c: Vertical(g10)
    c: Block(g10)
    c: Horizontal(g11)
    c: Block(g11)
    c: Coincident(g12,g10)
    c: Horizontal(g12)
    c: Block(g12)
    c: Coincident(g13,g11)
    c: Vertical(g13)
    c: Block(g13)
    c: Coincident(g14,g10)
    c: Horizontal(g14)
    c: Block(g14)
    c: Block(g9)
    c: Block(g1)
    c: Weight(g15) = 1
    c: Equal(g15,g16)
    c: Equal(g15,g17)
    c: InternalAlignment(g15,g18)
    c: InternalAlignment(g16,g18)
    c: InternalAlignment(g17,g18)
    c: InternalAlignment(g19,g18)
    c: InternalAlignment(g20,g18)
    c: Weight(g21) = 1
    c: Equal(g21,g22)
    c: Equal(g21,g23)
    c: InternalAlignment(g21,g24)
    c: InternalAlignment(g22,g24)
    c: InternalAlignment(g23,g24)
    c: InternalAlignment(g25,g24)
    c: InternalAlignment(g26,g24)
    c: Weight(g27) = 1
    c: Equal(g27,g28)
    c: Equal(g27,g29)
    c: Coincident(g30,g14)
    c: InternalAlignment(g27,g30)
    c: InternalAlignment(g28,g30)
    c: InternalAlignment(g29,g30)
    c: InternalAlignment(g31,g30)
    c: InternalAlignment(g32,g30)
    c: Coincident(g36,g12)
    c: Weight(g33) = 1
    c: Equal(g33,g34)
    c: Equal(g33,g35)
    c: Coincident(g36,g11)
    c: InternalAlignment(g33,g36)
    c: InternalAlignment(g34,g36)
    c: InternalAlignment(g35,g36)
    c: InternalAlignment(g37,g36)
    c: InternalAlignment(g38,g36)
    c: Coincident(g42,g13)
    c: Weight(g39) = 1
    c: Equal(g39,g40)
    c: Equal(g39,g41)
    c: Coincident(g42,g1)
    c: InternalAlignment(g39,g42)
    c: InternalAlignment(g40,g42)
    c: InternalAlignment(g41,g42)
    c: InternalAlignment(g43,g42)
    c: InternalAlignment(g44,g42)
    c: Block(g18)
    c: Block(g24)
    c: Block(g30)
    c: Block(g36)
    c: Block(g42)
    c: Horizontal(g45)
    c: Coincident(g45,g0)
    c: Vertical(g46)
    c: Coincident(g46,g45)
    c: Coincident(g47,g46)
    c: Coincident(g47,g18)
    c: Horizontal(g47)
    c: Block(g46)
    c: Coincident(g48,g18)
    c: Horizontal(g48)
    c: Distance(g48) = 1.33
    c: Vertical(g49)
    c: Coincident(g49,g48)
    c: Coincident(g50,g49)
    c: Coincident(g50,g24)
    c: Horizontal(g50)
    c: Tangent(g50,g22)
    c: Horizontal(g51)
    c: Coincident(g51,g24)
    c: Block(g51)
    c: Vertical(g52)
    c: Block(g52)
    c: Coincident(g52,g51)
    c: Coincident(g53,g52)
    c: Coincident(g53,g30)
    c: Horizontal(g53)
    c: Distance(g1) = 8.5
FEATURE [Part::Feature] Face024
  shape: bbox 9.8 x 26.5 x 2e-07 mm, 1 faces, 0 solids (baked)
FEATURE [Part::Revolution] Revolve024
  Angle = 360
  Axis = (0,1,0)
  Base = (0,0,0)
  FaceMakerClass = Part::FaceMakerBullseye
  Placement = pos=(0,0,0) rot=(0,0,1;1.5708rad)
  Solid = false
  Source = -> Face024
  Symmetric = false
FEATURE [Part::Feature] Face025
  shape: bbox 9.8 x 26.5 x 2e-07 mm, 1 faces, 0 solids (baked)
FEATURE [Part::Revolution] Revolve025
  Angle = 360
  Axis = (0,1,0)
  Base = (0,0,0)
  FaceMakerClass = Part::FaceMakerBullseye
  Placement = pos=(0,0,0) rot=(0,0,1;1.5708rad)
  Solid = false
  Source = -> Face025
  Symmetric = false
FEATURE [Part::MultiFuse] Fusion033
  Placement = pos=(-18,19,36) rot=(0,0,1;0rad)
  Shapes = -> [Revolve025,Revolve024]
FEATURE [Part::Cylinder] Cylinder014
  Angle = 360
  AttacherType = Attacher::AttachEngine3D
  Height = 20
  Placement = pos=(0,0,36.15) rot=(0,0,1;0rad)
  Radius = 14.3
FEATURE [Part::Cylinder] Cylinder015
  Angle = 360
  AttacherType = Attacher::AttachEngine3D
  Height = 10
  Placement = pos=(0,0,36.15) rot=(0,0,1;0rad)
  Radius = 4
FEATURE [Part::MultiFuse] Fusion034  label="removeToCreteHoleForPlugHousing004"
  Placement = pos=(-42,19,36) rot=(0,1,0;1.5708rad)
  Shapes = -> [Cylinder014,Cylinder015]
FEATURE [Part::Cut] Cut008  label="top004"
  Base = -> Cut004
  Placement = pos=(-1,0,0) rot=(0,0,1;0rad)
  Tool = -> Fusion034
FEATURE [Part::Box] Box005  label="Cube005"
  AttacherType = Attacher::AttachEngine3D
  Height = 28
  Length = 3
  Placement = pos=(110.7,19,22) rot=(0,0,1;0rad)
  Width = 15.7
FEATURE [Part::Cylinder] Cylinder016
  Angle = 360
  AttacherType = Attacher::AttachEngine3D
  Height = 10
  Placement = pos=(0,0,36.15) rot=(0,0,1;0rad)
  Radius = 4
FEATURE [Part::Cylinder] Cylinder017
  Angle = 360
  AttacherType = Attacher::AttachEngine3D
  Height = 20
  Placement = pos=(0,0,36.15) rot=(0,0,1;0rad)
  Radius = 10.3
FEATURE [Part::MultiFuse] Fusion035  label="removeToCreteHoleForPlugHousing005"
  Placement = pos=(70,19,36) rot=(0,1,0;1.5708rad)
  Shapes = -> [Cylinder017,Cylinder016]
FEATURE [Part::Cut] Cut009  label="plugHousingTab001"
  Base = -> Box005
  Placement = pos=(-107.4,-14,0) rot=(0,0,1;0rad)
  Tool = -> Fusion035
FEATURE [Part::Box] Box006  label="Cube006"
  AttacherType = Attacher::AttachEngine3D
  Height = 28
  Length = 3
  Placement = pos=(110.7,19,22) rot=(0,0,1;0rad)
  Width = 15.7
FEATURE [Part::Cylinder] Cylinder018
  Angle = 360
  AttacherType = Attacher::AttachEngine3D
  Height = 10
  Placement = pos=(0,0,36.15) rot=(0,0,1;0rad)
  Radius = 4
FEATURE [Part::Cylinder] Cylinder019
  Angle = 360
  AttacherType = Attacher::AttachEngine3D
  Height = 20
  Placement = pos=(0,0,36.15) rot=(0,0,1;0rad)
  Radius = 10.3
FEATURE [Part::MultiFuse] Fusion036  label="removeToCreteHoleForPlugHousing006"
  Placement = pos=(70,19,36) rot=(0,1,0;1.5708rad)
  Shapes = -> [Cylinder019,Cylinder018]
FEATURE [Part::Cut] Cut010  label="plugHousingTab002"
  Base = -> Box006
  Placement = pos=(-107.4,-14,0) rot=(0,0,1;0rad)
  Tool = -> Fusion036
FEATURE [Part::MultiFuse] Fusion037
  Placement = pos=(9.6,23,0) rot=(0,0,1;3.14159rad)
  Shapes = -> [Cut009,Cut010]
FEATURE [Part::Box] Box  label="Cube"
  AttacherType = Attacher::AttachEngine3D
  Height = 10
  Length = 3
  Placement = pos=(3.3,4,12) rot=(0,0,1;0rad)
  Width = 10
FEATURE [Part::Fillet] Fillet004
  Base = -> Fusion028
  Edges = 1 edges r=2: [Edge25]
FEATURE [Part::Fillet] Fillet005  label="plugHousing046"
  Base = -> Fillet004
  Edges = 1 edges r=2: [Edge8]
FEATURE [Part::Fillet] Fillet006
  Base = -> Box
  Edges = 1 edges r=2: [Edge11]
FEATURE [Part::Box] Box007  label="Cube007"
  AttacherType = Attacher::AttachEngine3D
  Height = 10
  Length = 3
  Placement = pos=(3.3,4,50) rot=(0,0,1;0rad)
  Width = 10
FEATURE [Part::Fillet] Fillet007
  Base = -> Box007
  Edges = 1 edges r=2: [Edge12]
FEATURE [Part::Box] Box008  label="Cube008"
  AttacherType = Attacher::AttachEngine3D
  Height = 28
  Length = 4
  Placement = pos=(5,0,22) rot=(0,0,1;0rad)
  Width = 10
FEATURE [Part::Fillet] Fillet008
  Base = -> Box008
  Edges = 1 edges r=1: [Edge7]
FEATURE [Part::Fillet] Fillet009
  Base = -> Fillet008
  Edges = 1 edges r=2: [Edge5]
FEATURE [Part::Fillet] Fillet010
  Base = -> Fillet009
  Edges = 1 edges r=2: [Edge2]
FEATURE [Sketcher::SketchObject] Sketch009  label="topSketch003"
  FullyConstrained = true
  sketch-geometry (4):
    g0: LineSegment StartX=16.8446 StartY=31.512 StartZ=0 EndX=16.3251 EndY=34.4666 EndZ=0
    g1: ArcOfCircle CenterX=19 CenterY=19.2524 CenterZ=0 NormalX=0 NormalY=0 NormalZ=1 AngleXU=0 Radius=15.4476 StartAngle=1.74483 EndAngle=2.72717
    g2: ArcOfCircle CenterX=19 CenterY=19.2524 CenterZ=0 NormalX=0 NormalY=0 NormalZ=1 AngleXU=0 Radius=12.4476 StartAngle=1.74483 EndAngle=2.73189
    g3: LineSegment StartX=4.86004 StartY=25.4725 StartZ=0 EndX=7.58253 EndY=24.2107 EndZ=0
  constraints (7):
    c: Block(g0)
    c: Coincident(g1,g0)
    c: Coincident(g2,g0)
    c: Coincident(g3,g1)
    c: Coincident(g3,g2)
    c: Block(g1)
    c: Block(g2)
FEATURE [Part::Extrusion] Extrude008
  Base = -> Sketch009
  Dir = (0,0,1)
  DirMode = 2
  FaceMakerClass = Part::FaceMakerBullseye
  LengthFwd = 10
  LengthRev = 0
  Placement = pos=(0,0,31) rot=(0,0,1;0rad)
  Solid = true
  Symmetric = false
FEATURE [Part::Cylinder] Cylinder020
  Angle = 360
  AttacherType = Attacher::AttachEngine3D
  Height = 20
  Placement = pos=(0,0,36.15) rot=(0,0,1;0rad)
  Radius = 8.2
FEATURE [Part::Cylinder] Cylinder021
  Angle = 360
  AttacherType = Attacher::AttachEngine3D
  Height = 10
  Placement = pos=(0,0,36.15) rot=(0,0,1;0rad)
  Radius = 4
FEATURE [Part::MultiFuse] Fusion038  label="removeToCreteHoleForPlugHousing007"
  Placement = pos=(-42,19,36) rot=(0,1,0;1.5708rad)
  Shapes = -> [Cylinder020,Cylinder021]
FEATURE [Part::Cut] Cut011
  Base = -> Extrude008
  Tool = -> Fusion038
FEATURE [Part::Fillet] Fillet011
  Base = -> Cut011
  Edges = 1 edges r=2: [Edge1]
FEATURE [Part::Fillet] Fillet012
  Base = -> Fillet011
  Edges = 1 edges r=2.5: [Edge1]
FEATURE [Part::Fillet] Fillet013
  Base = -> Fillet012
  Edges = 1 edges r=2.5: [Edge2]
FEATURE [Part::Box] Box010  label="Cube010"
  AttacherType = Attacher::AttachEngine3D
  Height = 16
  Length = 8
  Placement = pos=(12.7,31.52,28) rot=(0,0,1;0rad)
  Width = 4
FEATURE [Sketcher::SketchObject] Sketch010  label="topSketch004"
  FullyConstrained = true
  sketch-geometry (4):
    g0: LineSegment StartX=16.8446 StartY=31.512 StartZ=0 EndX=16.3251 EndY=34.4666 EndZ=0
    g1: ArcOfCircle CenterX=19 CenterY=19.2524 CenterZ=0 NormalX=0 NormalY=0 NormalZ=1 AngleXU=0 Radius=15.4476 StartAngle=1.74483 EndAngle=2.72717
    g2: ArcOfCircle CenterX=19 CenterY=19.2524 CenterZ=0 NormalX=0 NormalY=0 NormalZ=1 AngleXU=0 Radius=12.4476 StartAngle=1.74483 EndAngle=2.73189
    g3: LineSegment StartX=4.86004 StartY=25.4725 StartZ=0 EndX=7.58253 EndY=24.2107 EndZ=0
  constraints (7):
    c: Block(g0)
    c: Coincident(g1,g0)
    c: Coincident(g2,g0)
    c: Coincident(g3,g1)
    c: Coincident(g3,g2)
    c: Block(g1)
    c: Block(g2)
FEATURE [Part::Cylinder] Cylinder022
  Angle = 360
  AttacherType = Attacher::AttachEngine3D
  Height = 10
  Placement = pos=(0,0,36.15) rot=(0,0,1;0rad)
  Radius = 4
FEATURE [Sketcher::SketchObject] Sketch011  label="topSketch005"
  FullyConstrained = true
  sketch-geometry (4):
    g0: LineSegment StartX=16.8446 StartY=31.512 StartZ=0 EndX=16.3251 EndY=34.4666 EndZ=0
    g1: ArcOfCircle CenterX=19 CenterY=19.2524 CenterZ=0 NormalX=0 NormalY=0 NormalZ=1 AngleXU=0 Radius=15.4476 StartAngle=1.74483 EndAngle=2.72717
    g2: ArcOfCircle CenterX=19 CenterY=19.2524 CenterZ=0 NormalX=0 NormalY=0 NormalZ=1 AngleXU=0 Radius=12.4476 StartAngle=1.74483 EndAngle=2.73189
    g3: LineSegment StartX=4.86004 StartY=25.4725 StartZ=0 EndX=7.58253 EndY=24.2107 EndZ=0
  constraints (7):
    c: Block(g0)
    c: Coincident(g1,g0)
    c: Coincident(g2,g0)
    c: Coincident(g3,g1)
    c: Coincident(g3,g2)
    c: Block(g1)
    c: Block(g2)
FEATURE [Part::Extrusion] Extrude010
  Base = -> Sketch011
  Dir = (0,0,1)
  DirMode = 2
  FaceMakerClass = Part::FaceMakerBullseye
  LengthFwd = 10.6
  LengthRev = 0
  Placement = pos=(0,0,31) rot=(0,0,1;0rad)
  Solid = true
  Symmetric = false
FEATURE [Part::Cylinder] Cylinder023
  Angle = 360
  AttacherType = Attacher::AttachEngine3D
  Height = 20
  Placement = pos=(0,0,36.15) rot=(0,0,1;0rad)
  Radius = 8.2
FEATURE [Part::MultiFuse] Fusion039  label="removeToCreteHoleForPlugHousing008"
  Placement = pos=(-42,19,36) rot=(0,1,0;1.5708rad)
  Shapes = -> [Cylinder023,Cylinder022]
FEATURE [Part::Cut] Cut012
  Base = -> Extrude010
  Placement = pos=(0,0,-0.3) rot=(0,0,1;0rad)
  Tool = -> Fusion039
FEATURE [Part::Cut] Cut013
  Base = -> Box010
  Tool = -> Cut012
FEATURE [Part::Fillet] Fillet014
  Base = -> Cut013
  Edges = 1 edges r=0.7: [Edge13]
FEATURE [Part::Fillet] Fillet015
  Base = -> Fillet014
  Edges = 1 edges r=0.7: [Edge13]
FEATURE [Part::Fillet] Fillet016
  Base = -> Fillet015
  Edges = 1 edges r=0.7: [Edge16]
FEATURE [Part::Fillet] Fillet017
  Base = -> Fillet016
  Edges = 1 edges r=0.7: [Edge11]
FEATURE [Part::Fillet] Fillet018
  Base = -> Fillet017
  Edges = 1 edges r=0.7: [Edge10]
FEATURE [Part::Fillet] Fillet019
  Base = -> Fillet018
  Edges = 1 edges r=1.2: [Edge5]
FEATURE [Part::Fillet] Fillet020
  Base = -> Fillet019
  Edges = 1 edges r=1.2: [Edge12]
FEATURE [Part::Fillet] Fillet021
  Base = -> Fillet020
  Edges = 1 edges r=2: [Edge1]
  Placement = pos=(0.3,0,0) rot=(0,0,1;0rad)
FEATURE [Part::MultiFuse] Fusion040  label="top005"
  Shapes = -> [Cut008,Fillet021]
FEATURE [Part::MultiFuse] Fusion041  label="wireHolder"
  Shapes = -> [Fusion033,Fillet013]
FEATURE [Part::MultiFuse] Fusion042
  Shapes = -> [Fillet007,Fusion041]
FEATURE [Part::MultiFuse] Fusion043  label="wireHolder001"
  Shapes = -> [Fusion042,Fillet010]
FEATURE [Part::MultiFuse] Fusion044  label="wireHolder002"
  Shapes = -> [Fillet006,Fusion037,Fusion043]
FEATURE [Part::Feature] Face026
  shape: bbox 11 x 6 x 2e-07 mm, 1 faces, 0 solids (baked)
FEATURE [Part::Revolution] Revolve026
  Angle = 360
  Axis = (0,1,0)
  Base = (0,0,0)
  FaceMakerClass = Part::FaceMakerBullseye
  Placement = pos=(30.3,-1,19.7) rot=(0,0,1;0rad)
  Solid = false
  Source = -> Face026
  Symmetric = false
FEATURE [Sketcher::SketchObject] Sketch013  label="topSketch006"
  FullyConstrained = true
  sketch-geometry (13):
    g0: LineSegment StartX=117 StartY=19 StartZ=0 EndX=117 EndY=38 EndZ=0
    g1: ArcOfCircle CenterX=98 CenterY=19 CenterZ=0 NormalX=0 NormalY=0 NormalZ=1 AngleXU=0 Radius=19 StartAngle=5.7297 EndAngle=6.28319
    g2: LineSegment StartX=0 StartY=3 StartZ=0 EndX=0 EndY=19 EndZ=0
    g3: LineSegment StartX=19 StartY=38 StartZ=0 EndX=117 EndY=38 EndZ=0
    g4: ArcOfCircle CenterX=19 CenterY=19 CenterZ=0 NormalX=0 NormalY=0 NormalZ=1 AngleXU=0 Radius=19 StartAngle=1.5708 EndAngle=3.14159
    g5: ArcOfCircle CenterX=19 CenterY=19 CenterZ=0 NormalX=0 NormalY=0 NormalZ=1 AngleXU=0 Radius=16 StartAngle=1.5708 EndAngle=3.14159
    g6: ArcOfCircle CenterX=98 CenterY=19 CenterZ=0 NormalX=0 NormalY=0 NormalZ=1 AngleXU=0 Radius=16 StartAngle=5.60905 EndAngle=6.28319
    g7: LineSegment StartX=114 StartY=19 StartZ=0 EndX=114 EndY=35 EndZ=0
    g8: LineSegment StartX=110.5 StartY=9.01251 StartZ=0 EndX=114.163 EndY=9.01251 EndZ=0
    g9: LineSegment StartX=114 StartY=35 StartZ=0 EndX=19 EndY=35 EndZ=0
    g10: LineSegment StartX=0 StartY=3 StartZ=0 EndX=0 EndY=0 EndZ=0
    g11: LineSegment StartX=3 StartY=0 StartZ=0 EndX=0 EndY=0 EndZ=0
    g12: LineSegment StartX=3 StartY=19 StartZ=0 EndX=3 EndY=0 EndZ=0
  constraints (33):
    c: Vertical(g0)
    c: Distance(g0) = 19
    c: Block(g0)
    c: Coincident(g1,g0)
    c: Block(g1)
    c: Vertical(g2)
    c: Block(g2)
    c: Coincident(g3,g0)
    c: Horizontal(g3)
    c: Distance(g3) = 98
    c: Coincident(g4,g3)
    c: Coincident(g4,g2)
    c: Block(g4)
    c: Coincident(g5,g4)
    c: Coincident(g6,g1)
    c: Block(g6)
    c: Block(g5)
    c: Coincident(g7,g6)
    c: Vertical(g7)
    c: Coincident(g8,g6)
    c: Coincident(g8,g1)
    c: Coincident(g9,g7)
    c: Coincident(g9,g5)
    c: Horizontal(g9)
    c: Tangent(g9,g5)
    c: Coincident(g10,g2)
    c: Distance(g10) = 3
    c: Vertical(g10)
    c: Coincident(g11,g10)
    c: Horizontal(g11)
    c: Coincident(g12,g5)
    c: Coincident(g12,g11)
    c: Vertical(g12)
FEATURE [Part::Extrusion] Extrude011  label="top006"
  Base = -> Sketch013
  Dir = (0,0,1)
  DirMode = 2
  FaceMakerClass = Part::FaceMakerBullseye
  LengthFwd = 72
  LengthRev = 0
  Solid = true
  Symmetric = false
FEATURE [Sketcher::SketchObject] Sketch014
  FullyConstrained = true
  MapMode = 3
  Placement = pos=(0,0,0) rot=(1,0,0;1.5708rad)
  Support = -> [Extrude011]
  sketch-geometry (8):
    g0: Circle CenterX=80.351 CenterY=-67.6202 CenterZ=0 NormalX=0 NormalY=0 NormalZ=1 AngleXU=0 Radius=2
    g1: Circle CenterX=80.351 CenterY=-67.6202 CenterZ=0 NormalX=0 NormalY=0 NormalZ=1 AngleXU=0 Radius=3
    g2: Circle CenterX=80.351 CenterY=-4.92017 CenterZ=0 NormalX=0 NormalY=0 NormalZ=1 AngleXU=0 Radius=2
    g3: Circle CenterX=80.351 CenterY=-4.92017 CenterZ=0 NormalX=0 NormalY=0 NormalZ=1 AngleXU=0 Radius=3
    g4: Circle CenterX=23.851 CenterY=-4.92017 CenterZ=0 NormalX=0 NormalY=0 NormalZ=1 AngleXU=0 Radius=2
    g5: Circle CenterX=23.851 CenterY=-4.92017 CenterZ=0 NormalX=0 NormalY=0 NormalZ=1 AngleXU=0 Radius=3
    g6: Circle CenterX=23.851 CenterY=-67.6202 CenterZ=0 NormalX=0 NormalY=0 NormalZ=1 AngleXU=0 Radius=2
    g7: Circle CenterX=23.851 CenterY=-67.6202 CenterZ=0 NormalX=0 NormalY=0 NormalZ=1 AngleXU=0 Radius=3
  constraints (8):
    c: Block(g3)
    c: Block(g2)
    c: Block(g1)
    c: Block(g0)
    c: Block(g6)
    c: Block(g7)
    c: Block(g4)
    c: Block(g5)
FEATURE [Part::Feature] Face027
  shape: bbox 11 x 6 x 2e-07 mm, 1 faces, 0 solids (baked)
FEATURE [Part::Revolution] Revolve027
  Angle = 360
  Axis = (0,1,0)
  Base = (0,0,0)
  FaceMakerClass = Part::FaceMakerBullseye
  Placement = pos=(30.3,-1,51.7) rot=(0,0,1;0rad)
  Solid = false
  Source = -> Face027
  Symmetric = false
FEATURE [Part::Feature] Face028
  shape: bbox 11 x 6 x 2e-07 mm, 1 faces, 0 solids (baked)
FEATURE [Part::Revolution] Revolve028
  Angle = 360
  Axis = (0,1,0)
  Base = (0,0,0)
  FaceMakerClass = Part::FaceMakerBullseye
  Placement = pos=(62.3,-1,19.7) rot=(0,0,1;0rad)
  Solid = false
  Source = -> Face028
  Symmetric = false
FEATURE [Part::Feature] Face029
  shape: bbox 11 x 6 x 2e-07 mm, 1 faces, 0 solids (baked)
FEATURE [Part::Revolution] Revolve029
  Angle = 360
  Axis = (0,1,0)
  Base = (0,0,0)
  FaceMakerClass = Part::FaceMakerBullseye
  Placement = pos=(62.3,-1,51.7) rot=(0,0,1;0rad)
  Solid = false
  Source = -> Face029
  Symmetric = false
FEATURE [Part::Feature] Wire
  shape: bbox 11 x 5.2 x 2e-07 mm, 0 faces, 0 solids (baked)
FEATURE [Part::Revolution] Revolve030
  Angle = 360
  Axis = (0,1,0)
  Base = (0,0,0)
  FaceMakerClass = Part::FaceMakerBullseye
  Placement = pos=(30.3,38,19.7) rot=(0,0,1;0rad)
  Solid = true
  Source = -> Wire
  Symmetric = false
FEATURE [Part::Feature] Wire001
  shape: bbox 11 x 5.2 x 2e-07 mm, 0 faces, 0 solids (baked)
FEATURE [Part::Revolution] Revolve031
  Angle = 360
  Axis = (0,1,0)
  Base = (0,0,0)
  FaceMakerClass = Part::FaceMakerBullseye
  Placement = pos=(30.3,38,51.7) rot=(0,0,1;0rad)
  Solid = true
  Source = -> Wire001
  Symmetric = false
FEATURE [Part::Feature] Wire002
  shape: bbox 11 x 5.2 x 2e-07 mm, 0 faces, 0 solids (baked)
FEATURE [Part::Revolution] Revolve032
  Angle = 360
  Axis = (0,1,0)
  Base = (0,0,0)
  FaceMakerClass = Part::FaceMakerBullseye
  Placement = pos=(62.3,38,51.7) rot=(0,0,1;0rad)
  Solid = true
  Source = -> Wire002
  Symmetric = false
FEATURE [Part::Feature] Wire003
  shape: bbox 11 x 5.2 x 2e-07 mm, 0 faces, 0 solids (baked)
FEATURE [Part::Revolution] Revolve033
  Angle = 360
  Axis = (0,1,0)
  Base = (0,0,0)
  FaceMakerClass = Part::FaceMakerBullseye
  Placement = pos=(62.3,38,19.7) rot=(0,0,1;0rad)
  Solid = true
  Source = -> Wire003
  Symmetric = false
FEATURE [Part::MultiFuse] Fusion045  label="altRandScrewHousing"
  Shapes = -> [Revolve029,Revolve027,Revolve028,Revolve026]
FEATURE [Part::MultiFuse] Fusion046  label="fanScrewHousing"
  Shapes = -> [Revolve033,Revolve032,Revolve031,Revolve030]
FEATURE [Sketcher::SketchObject] Sketch015
  FullyConstrained = true
  sketch-geometry (17):
    g0: Circle CenterX=-3.5 CenterY=23.5 CenterZ=0 NormalX=0 NormalY=0 NormalZ=1 AngleXU=0 Radius=1
    g1: Circle CenterX=-1 CenterY=15.25 CenterZ=0 NormalX=0 NormalY=0 NormalZ=1 AngleXU=0 Radius=1
    g2: Circle CenterX=-3.5 CenterY=7 CenterZ=0 NormalX=0 NormalY=0 NormalZ=1 AngleXU=0 Radius=1
    g3: BSplineCurve PolesCount=3 KnotsCount=2 Degree=2 IsPeriodic=0
    g4: GeomPoint X=-3.5 Y=23.5 Z=0
    g5: GeomPoint X=-3.5 Y=7 Z=0
    g6: Circle CenterX=-4.8 CenterY=30.5 CenterZ=0 NormalX=0 NormalY=0 NormalZ=1 AngleXU=0 Radius=1
    g7: Circle CenterX=-3.5 CenterY=30.5 CenterZ=0 NormalX=0 NormalY=0 NormalZ=1 AngleXU=0 Radius=1
    g8: Circle CenterX=-3.5 CenterY=29.2 CenterZ=0 NormalX=0 NormalY=0 NormalZ=1 AngleXU=0 Radius=1
    g9: BSplineCurve PolesCount=3 KnotsCount=2 Degree=2 IsPeriodic=0
    g10: GeomPoint X=-4.8 Y=30.5 Z=0
    g11: GeomPoint X=-3.5 Y=29.2 Z=0
    g12: LineSegment StartX=-3.5 StartY=29.2 StartZ=0 EndX=-3.5 EndY=23.5 EndZ=0
    g13: LineSegment StartX=-4.8 StartY=30.5 StartZ=0 EndX=0 EndY=30.5 EndZ=0
    g14: LineSegment StartX=-3.5 StartY=0.3 StartZ=0 EndX=0 EndY=0.3 EndZ=0
    g15: LineSegment StartX=-3.5 StartY=0.3 StartZ=0 EndX=-3.5 EndY=7 EndZ=0
    g16: LineSegment StartX=0 StartY=0.3 StartZ=0 EndX=0 EndY=30.5 EndZ=0
  constraints (33):
    c: Weight(g0) = 1
    c: Equal(g0,g1)
    c: Equal(g0,g2)
    c: InternalAlignment(g0,g3)
    c: InternalAlignment(g1,g3)
    c: InternalAlignment(g2,g3)
    c: InternalAlignment(g4,g3)
    c: InternalAlignment(g5,g3)
    c: Block(g3)
    c: Weight(g6) = 1
    c: Equal(g6,g7)
    c: Equal(g6,g8)
    c: InternalAlignment(g6,g9)
    c: InternalAlignment(g7,g9)
    c: InternalAlignment(g8,g9)
    c: InternalAlignment(g10,g9)
    c: InternalAlignment(g11,g9)
    c: Block(g9)
    c: Coincident(g12,g9)
    c: Coincident(g12,g3)
    c: Vertical(g12)
    c: Coincident(g13,g9)
    c: Horizontal(g13)
    c: Distance(g13) = 4.8
    c: Horizontal(g14)
    c: Block(g14)
    c: Coincident(g15,g14)
    c: Coincident(g15,g3)
    c: Vertical(g15)
    c: Coincident(g16,g14)
    c: Coincident(g16,g13)
    c: Vertical(g16)
    c: Tangent(g16,g1)
FEATURE [Sketcher::SketchObject] Sketch016
  FullyConstrained = true
  sketch-geometry (16):
    g0: Circle CenterX=-3.5 CenterY=23.5 CenterZ=0 NormalX=0 NormalY=0 NormalZ=1 AngleXU=0 Radius=1
    g1: Circle CenterX=-1 CenterY=15.25 CenterZ=0 NormalX=0 NormalY=0 NormalZ=1 AngleXU=0 Radius=1
    g2: Circle CenterX=-3.5 CenterY=7 CenterZ=0 NormalX=0 NormalY=0 NormalZ=1 AngleXU=0 Radius=1
    g3: BSplineCurve PolesCount=3 KnotsCount=2 Degree=2 IsPeriodic=0
    g4: GeomPoint X=-3.5 Y=23.5 Z=0
    g5: GeomPoint X=-3.5 Y=7 Z=0
    g6: LineSegment StartX=-3.5 StartY=28.2 StartZ=0 EndX=-3.5 EndY=23.5 EndZ=0
    g7: LineSegment StartX=0 StartY=29.5 StartZ=0 EndX=0 EndY=30 EndZ=0
    g8: LineSegment StartX=-3.5 StartY=28.2 StartZ=0 EndX=-3.5 EndY=30 EndZ=0
    g9: LineSegment StartX=0 StartY=30 StartZ=0 EndX=0 EndY=30.5 EndZ=0
    g10: LineSegment StartX=0 StartY=30.5 StartZ=0 EndX=-3.5 EndY=30.5 EndZ=0
    g11: LineSegment StartX=-3.5 StartY=30.5 StartZ=0 EndX=-3.5 EndY=30 EndZ=0
    g12: LineSegment StartX=0 StartY=29.5 StartZ=0 EndX=0 EndY=5 EndZ=0
    g13: LineSegment StartX=-3.5 StartY=0.3 StartZ=0 EndX=-3.5 EndY=7 EndZ=0
    g14: LineSegment StartX=-3.5 StartY=0.3 StartZ=0 EndX=0 EndY=0.3 EndZ=0
    g15: LineSegment StartX=0 StartY=5 StartZ=0 EndX=0 EndY=0.3 EndZ=0
  constraints (39):
    c: Weight(g0) = 1
    c: Equal(g0,g1)
    c: Equal(g0,g2)
    c: InternalAlignment(g0,g3)
    c: InternalAlignment(g1,g3)
    c: InternalAlignment(g2,g3)
    c: InternalAlignment(g4,g3)
    c: InternalAlignment(g5,g3)
    c: Block(g3)
    c: Coincident(g6,g3)
    c: Vertical(g6)
    c: Vertical(g7)
    c: Distance(g7) = 0.5
    c: Coincident(g8,g6)
    c: Vertical(g8)
    c: Block(g6)
    c: Block(g7)
    c: Vertical(g9)
    c: Equal(g7,g9) = 0.5
    c: Block(g9)
    c: Coincident(g9,g7)
    c: Horizontal(g10)
    c: Coincident(g10,g9)
    c: Coincident(g11,g10)
    c: Coincident(g11,g8)
    c: Vertical(g11)
    c: Block(g11)
    c: Coincident(g12,g7)
    c: Vertical(g12)
    c: Coincident(g13,g3)
    c: Vertical(g13)
    c: Distance(g13) = 6.7
    c: Coincident(g14,g13)
    c: Horizontal(g14)
    c: Block(g14)
    c: Coincident(g15,g12)
    c: Coincident(g15,g14)
    c: Vertical(g15)
    c: Block(g15)
FEATURE [Sketcher::SketchObject] Sketch017
  FullyConstrained = true
  sketch-geometry (11):
    g0: LineSegment StartX=-3.5 StartY=1e-16 StartZ=0 EndX=-1.6 EndY=1e-16 EndZ=0
    g1: LineSegment StartX=-1.6 StartY=1e-16 StartZ=0 EndX=-1.6 EndY=1.5 EndZ=0
    g2: LineSegment StartX=-3.5 StartY=1.5 StartZ=0 EndX=-1.6 EndY=1.5 EndZ=0
    g3: LineSegment StartX=-3.5 StartY=1e-16 StartZ=0 EndX=-4.8 EndY=1e-16 EndZ=0
    g4: Circle CenterX=-3.5 CenterY=1.3 CenterZ=0 NormalX=0 NormalY=0 NormalZ=1 AngleXU=0 Radius=1
    g5: Circle CenterX=-3.5 CenterY=1e-16 CenterZ=0 NormalX=0 NormalY=0 NormalZ=1 AngleXU=0 Radius=1
    g6: Circle CenterX=-4.8 CenterY=1e-16 CenterZ=0 NormalX=0 NormalY=0 NormalZ=1 AngleXU=0 Radius=1
    g7: BSplineCurve PolesCount=3 KnotsCount=2 Degree=2 IsPeriodic=0
    g8: GeomPoint X=-3.5 Y=1.3 Z=0
    g9: GeomPoint X=-4.8 Y=1e-16 Z=0
    g10: LineSegment StartX=-3.5 StartY=1.3 StartZ=0 EndX=-3.5 EndY=1.5 EndZ=0
  constraints (24):
    c: Horizontal(g0)
    c: Distance(g0) = 1.9
    c: Block(g0)
    c: Coincident(g1,g0)
    c: Vertical(g1)
    c: Coincident(g2,g1)
    c: Horizontal(g2)
    c: Coincident(g3,g0)
    c: Horizontal(g3)
    c: Distance(g3) = 1.3
    c: Weight(g4) = 1
    c: Equal(g4,g5)
    c: Coincident(g5,g0)
    c: Equal(g4,g6)
    c: Coincident(g7,g3)
    c: InternalAlignment(g4,g7)
    c: InternalAlignment(g5,g7)
    c: InternalAlignment(g6,g7)
    c: InternalAlignment(g8,g7)
    c: InternalAlignment(g9,g7)
    c: Coincident(g10,g7)
    c: Coincident(g10,g2)
    c: Vertical(g10)
    c: Block(g10)
FEATURE [Part::Feature] Face035
  shape: bbox 3.2 x 1.5 x 2e-07 mm, 1 faces, 0 solids (baked)
FEATURE [Part::Revolution] Revolve039  label="backCaseScrewRetainer"
  Angle = 360
  Axis = (0,1,0)
  Base = (0,0,0)
  FaceMakerClass = Part::FaceMakerBullseye
  Placement = pos=(12.5,3,62) rot=(0,0,1;0rad)
  Solid = false
  Source = -> Face035
  Symmetric = false
FEATURE [Part::Feature] Face036
  shape: bbox 3.2 x 1.5 x 2e-07 mm, 1 faces, 0 solids (baked)
FEATURE [Part::Feature] Face039
  shape: bbox 4.8 x 30.2 x 2e-07 mm, 1 faces, 0 solids (baked)
FEATURE [Part::Revolution] Revolve043  label="frontCaseScrewPost002"
  Angle = 360
  Axis = (0,1,0)
  Base = (0,0,0)
  FaceMakerClass = Part::FaceMakerBullseye
  Placement = pos=(89.5,4.5,3.5) rot=(0,0,1;0rad)
  Solid = false
  Source = -> Face039
  Symmetric = false
FEATURE [Part::Feature] Face042
  shape: bbox 4.8 x 30.2 x 2e-07 mm, 1 faces, 0 solids (baked)
FEATURE [Part::Revolution] Revolve046  label="frontCaseScrewPost003"
  Angle = 360
  Axis = (0,1,0)
  Base = (0,0,0)
  FaceMakerClass = Part::FaceMakerBullseye
  Placement = pos=(89.5,4.5,68.5) rot=(0,0,1;0rad)
  Solid = false
  Source = -> Face042
  Symmetric = false
FEATURE [Part::Feature] Face043
  shape: bbox 3.2 x 1.5 x 2e-07 mm, 1 faces, 0 solids (baked)
FEATURE [Part::Revolution] Revolve047  label="frontCaseScrewRetainer002"
  Angle = 360
  Axis = (0,1,0)
  Base = (0,0,0)
  FaceMakerClass = Part::FaceMakerBullseye
  Placement = pos=(89.5,3,68.5) rot=(0,0,1;0rad)
  Solid = false
  Source = -> Face043
  Symmetric = false
FEATURE [Part::Feature] Face044
  shape: bbox 3.2 x 1.5 x 2e-07 mm, 1 faces, 0 solids (baked)
FEATURE [Part::Revolution] Revolve048  label="frontCaseScrewRetainer003"
  Angle = 360
  Axis = (0,1,0)
  Base = (0,0,0)
  FaceMakerClass = Part::FaceMakerBullseye
  Placement = pos=(89.5,3,3.5) rot=(0,0,1;0rad)
  Solid = false
  Source = -> Face044
  Symmetric = false
FEATURE [App::MeasureDistance] Distance002  label="Distance: 1.67 mm"
  Distance = 1.66921
  P1 = (99.2361,4.7524,71.7)
  P2 = (99.2347,6.42161,71.7)
FEATURE [Sketcher::SketchObject] Sketch018
  FullyConstrained = true
  sketch-geometry (7):
    g0: LineSegment StartX=0 StartY=0 StartZ=0 EndX=0 EndY=6 EndZ=0
    g1: Circle CenterX=0 CenterY=0 CenterZ=0 NormalX=0 NormalY=0 NormalZ=1 AngleXU=0 Radius=1
    g2: Circle CenterX=8 CenterY=6 CenterZ=0 NormalX=0 NormalY=0 NormalZ=1 AngleXU=0 Radius=1
    g3: BSplineCurve PolesCount=3 KnotsCount=2 Degree=2 IsPeriodic=0
    g4: GeomPoint X=0 Y=0 Z=0
    g5: GeomPoint X=8 Y=6 Z=0
    g6: LineSegment StartX=0 StartY=6 StartZ=0 EndX=8 EndY=6 EndZ=0
  constraints (14):
    c: Coincident(g0,g-1)
    c: Distance(g0) = 6
    c: Vertical(g0)
    c: Coincident(g3,g0)
    c: Weight(g1) = 1
    c: Equal(g1,g2)
    c: InternalAlignment(g1,g3)
    c: InternalAlignment(g2,g3)
    c: InternalAlignment(g4,g3)
    c: InternalAlignment(g5,g3)
    c: Block(g3)
    c: Coincident(g6,g0)
    c: Coincident(g6,g3)
    c: Horizontal(g6)
FEATURE [Part::Extrusion] Extrude012  label="caseScrewPillarBracket"
  Base = -> Sketch018
  Dir = (0,0,1)
  DirMode = 2
  FaceMakerClass = Part::FaceMakerBullseye
  LengthFwd = 2.4
  LengthRev = 0
  Placement = pos=(15.76,29,8.8) rot=(0,1,0;0rad)
  Solid = true
  Symmetric = false
FEATURE [Sketcher::SketchObject] Sketch019
  FullyConstrained = true
  sketch-geometry (7):
    g0: LineSegment StartX=0 StartY=0 StartZ=0 EndX=0 EndY=6 EndZ=0
    g1: Circle CenterX=0 CenterY=0 CenterZ=0 NormalX=0 NormalY=0 NormalZ=1 AngleXU=0 Radius=1
    g2: Circle CenterX=8 CenterY=6 CenterZ=0 NormalX=0 NormalY=0 NormalZ=1 AngleXU=0 Radius=1
    g3: BSplineCurve PolesCount=3 KnotsCount=2 Degree=2 IsPeriodic=0
    g4: GeomPoint X=0 Y=0 Z=0
    g5: GeomPoint X=8 Y=6 Z=0
    g6: LineSegment StartX=0 StartY=6 StartZ=0 EndX=8 EndY=6 EndZ=0
  constraints (14):
    c: Coincident(g0,g-1)
    c: Distance(g0) = 6
    c: Vertical(g0)
    c: Coincident(g3,g0)
    c: Weight(g1) = 1
    c: Equal(g1,g2)
    c: InternalAlignment(g1,g3)
    c: InternalAlignment(g2,g3)
    c: InternalAlignment(g4,g3)
    c: InternalAlignment(g5,g3)
    c: Block(g3)
    c: Coincident(g6,g0)
    c: Coincident(g6,g3)
    c: Horizontal(g6)
FEATURE [Part::Extrusion] Extrude013  label="caseScrewPillarBracket001"
  Base = -> Sketch019
  Dir = (0,0,1)
  DirMode = 2
  FaceMakerClass = Part::FaceMakerBullseye
  LengthFwd = 2.4
  LengthRev = 0
  Placement = pos=(15.76,29,60.8) rot=(0,0,1;0rad)
  Solid = true
  Symmetric = false
FEATURE [Sketcher::SketchObject] Sketch020
  FullyConstrained = true
  sketch-geometry (7):
    g0: LineSegment StartX=0 StartY=0 StartZ=0 EndX=0 EndY=6 EndZ=0
    g1: Circle CenterX=0 CenterY=0 CenterZ=0 NormalX=0 NormalY=0 NormalZ=1 AngleXU=0 Radius=1
    g2: Circle CenterX=8 CenterY=6 CenterZ=0 NormalX=0 NormalY=0 NormalZ=1 AngleXU=0 Radius=1
    g3: BSplineCurve PolesCount=3 KnotsCount=2 Degree=2 IsPeriodic=0
    g4: GeomPoint X=0 Y=0 Z=0
    g5: GeomPoint X=8 Y=6 Z=0
    g6: LineSegment StartX=0 StartY=6 StartZ=0 EndX=8 EndY=6 EndZ=0
  constraints (14):
    c: Coincident(g0,g-1)
    c: Distance(g0) = 6
    c: Vertical(g0)
    c: Coincident(g3,g0)
    c: Weight(g1) = 1
    c: Equal(g1,g2)
    c: InternalAlignment(g1,g3)
    c: InternalAlignment(g2,g3)
    c: InternalAlignment(g4,g3)
    c: InternalAlignment(g5,g3)
    c: Block(g3)
    c: Coincident(g6,g0)
    c: Coincident(g6,g3)
    c: Horizontal(g6)
FEATURE [Part::Extrusion] Extrude014  label="caseScrewPillarBracket002"
  Base = -> Sketch020
  Dir = (0,0,1)
  DirMode = 2
  FaceMakerClass = Part::FaceMakerBullseye
  LengthFwd = 2.4
  LengthRev = 0
  Placement = pos=(13.7,29,13.26) rot=(0,1,0;-1.5708rad)
  Solid = true
  Symmetric = false
FEATURE [Sketcher::SketchObject] Sketch021
  FullyConstrained = true
  sketch-geometry (7):
    g0: LineSegment StartX=0 StartY=0 StartZ=0 EndX=0 EndY=6 EndZ=0
    g1: Circle CenterX=0 CenterY=0 CenterZ=0 NormalX=0 NormalY=0 NormalZ=1 AngleXU=0 Radius=1
    g2: Circle CenterX=8 CenterY=6 CenterZ=0 NormalX=0 NormalY=0 NormalZ=1 AngleXU=0 Radius=1
    g3: BSplineCurve PolesCount=3 KnotsCount=2 Degree=2 IsPeriodic=0
    g4: GeomPoint X=0 Y=0 Z=0
    g5: GeomPoint X=8 Y=6 Z=0
    g6: LineSegment StartX=0 StartY=6 StartZ=0 EndX=8 EndY=6 EndZ=0
  constraints (14):
    c: Coincident(g0,g-1)
    c: Distance(g0) = 6
    c: Vertical(g0)
    c: Coincident(g3,g0)
    c: Weight(g1) = 1
    c: Equal(g1,g2)
    c: InternalAlignment(g1,g3)
    c: InternalAlignment(g2,g3)
    c: InternalAlignment(g4,g3)
    c: InternalAlignment(g5,g3)
    c: Block(g3)
    c: Coincident(g6,g0)
    c: Coincident(g6,g3)
    c: Horizontal(g6)
FEATURE [Part::Extrusion] Extrude015  label="caseScrewPillarBracket003"
  Base = -> Sketch021
  Dir = (0,0,1)
  DirMode = 2
  FaceMakerClass = Part::FaceMakerBullseye
  LengthFwd = 2.4
  LengthRev = 0
  Placement = pos=(11.3,29,58.74) rot=(0,1,0;1.5708rad)
  Solid = true
  Symmetric = false
FEATURE [Sketcher::SketchObject] Sketch022
  FullyConstrained = true
  sketch-geometry (7):
    g0: LineSegment StartX=0 StartY=0 StartZ=0 EndX=0 EndY=6 EndZ=0
    g1: Circle CenterX=0 CenterY=0 CenterZ=0 NormalX=0 NormalY=0 NormalZ=1 AngleXU=0 Radius=1
    g2: Circle CenterX=8 CenterY=6 CenterZ=0 NormalX=0 NormalY=0 NormalZ=1 AngleXU=0 Radius=1
    g3: BSplineCurve PolesCount=3 KnotsCount=2 Degree=2 IsPeriodic=0
    g4: GeomPoint X=0 Y=0 Z=0
    g5: GeomPoint X=8 Y=6 Z=0
    g6: LineSegment StartX=0 StartY=6 StartZ=0 EndX=8 EndY=6 EndZ=0
  constraints (14):
    c: Coincident(g0,g-1)
    c: Distance(g0) = 6
    c: Vertical(g0)
    c: Coincident(g3,g0)
    c: Weight(g1) = 1
    c: Equal(g1,g2)
    c: InternalAlignment(g1,g3)
    c: InternalAlignment(g2,g3)
    c: InternalAlignment(g4,g3)
    c: InternalAlignment(g5,g3)
    c: Block(g3)
    c: Coincident(g6,g0)
    c: Coincident(g6,g3)
    c: Horizontal(g6)
FEATURE [Part::Extrusion] Extrude016  label="caseScrewPillarBracket004"
  Base = -> Sketch022
  Dir = (0,0,1)
  DirMode = 2
  FaceMakerClass = Part::FaceMakerBullseye
  LengthFwd = 2.4
  LengthRev = 0
  Placement = pos=(88.3,29,65.23) rot=(0,1,0;1.5708rad)
  Solid = true
  Symmetric = false
FEATURE [Sketcher::SketchObject] Sketch023
  FullyConstrained = true
  sketch-geometry (7):
    g0: LineSegment StartX=0 StartY=0 StartZ=0 EndX=0 EndY=6 EndZ=0
    g1: Circle CenterX=0 CenterY=0 CenterZ=0 NormalX=0 NormalY=0 NormalZ=1 AngleXU=0 Radius=1
    g2: Circle CenterX=8 CenterY=6 CenterZ=0 NormalX=0 NormalY=0 NormalZ=1 AngleXU=0 Radius=1
    g3: BSplineCurve PolesCount=3 KnotsCount=2 Degree=2 IsPeriodic=0
    g4: GeomPoint X=0 Y=0 Z=0
    g5: GeomPoint X=8 Y=6 Z=0
    g6: LineSegment StartX=0 StartY=6 StartZ=0 EndX=8 EndY=6 EndZ=0
  constraints (14):
    c: Coincident(g0,g-1)
    c: Distance(g0) = 6
    c: Vertical(g0)
    c: Coincident(g3,g0)
    c: Weight(g1) = 1
    c: Equal(g1,g2)
    c: InternalAlignment(g1,g3)
    c: InternalAlignment(g2,g3)
    c: InternalAlignment(g4,g3)
    c: InternalAlignment(g5,g3)
    c: Block(g3)
    c: Coincident(g6,g0)
    c: Coincident(g6,g3)
    c: Horizontal(g6)
FEATURE [Part::Extrusion] Extrude017  label="caseScrewPillarBracket005"
  Base = -> Sketch023
  Dir = (0,0,1)
  DirMode = 2
  FaceMakerClass = Part::FaceMakerBullseye
  LengthFwd = 2.4
  LengthRev = 0
  Placement = pos=(90.7,29,6.77) rot=(0,-1,0;1.5708rad)
  Solid = true
  Symmetric = false
FEATURE [Sketcher::SketchObject] Sketch024
  FullyConstrained = true
  sketch-geometry (7):
    g0: LineSegment StartX=0 StartY=0 StartZ=0 EndX=0 EndY=6 EndZ=0
    g1: Circle CenterX=0 CenterY=0 CenterZ=0 NormalX=0 NormalY=0 NormalZ=1 AngleXU=0 Radius=1
    g2: Circle CenterX=8 CenterY=6 CenterZ=0 NormalX=0 NormalY=0 NormalZ=1 AngleXU=0 Radius=1
    g3: BSplineCurve PolesCount=3 KnotsCount=2 Degree=2 IsPeriodic=0
    g4: GeomPoint X=0 Y=0 Z=0
    g5: GeomPoint X=8 Y=6 Z=0
    g6: LineSegment StartX=0 StartY=6 StartZ=0 EndX=8 EndY=6 EndZ=0
  constraints (14):
    c: Coincident(g0,g-1)
    c: Distance(g0) = 6
    c: Vertical(g0)
    c: Coincident(g3,g0)
    c: Weight(g1) = 1
    c: Equal(g1,g2)
    c: InternalAlignment(g1,g3)
    c: InternalAlignment(g2,g3)
    c: InternalAlignment(g4,g3)
    c: InternalAlignment(g5,g3)
    c: Block(g3)
    c: Coincident(g6,g0)
    c: Coincident(g6,g3)
    c: Horizontal(g6)
FEATURE [Part::Extrusion] Extrude018  label="caseScrewPillarBracket006"
  Base = -> Sketch024
  Dir = (0,0,1)
  DirMode = 2
  FaceMakerClass = Part::FaceMakerBullseye
  LengthFwd = 2.4
  LengthRev = 0
  Placement = pos=(103.7,29,6.77) rot=(0,-1,0;1.5708rad)
  Solid = true
  Symmetric = false
FEATURE [Sketcher::SketchObject] Sketch025
  FullyConstrained = true
  sketch-geometry (7):
    g0: LineSegment StartX=0 StartY=0 StartZ=0 EndX=0 EndY=6 EndZ=0
    g1: Circle CenterX=0 CenterY=0 CenterZ=0 NormalX=0 NormalY=0 NormalZ=1 AngleXU=0 Radius=1
    g2: Circle CenterX=8 CenterY=6 CenterZ=0 NormalX=0 NormalY=0 NormalZ=1 AngleXU=0 Radius=1
    g3: BSplineCurve PolesCount=3 KnotsCount=2 Degree=2 IsPeriodic=0
    g4: GeomPoint X=0 Y=0 Z=0
    g5: GeomPoint X=8 Y=6 Z=0
    g6: LineSegment StartX=0 StartY=6 StartZ=0 EndX=8 EndY=6 EndZ=0
  constraints (14):
    c: Coincident(g0,g-1)
    c: Distance(g0) = 6
    c: Vertical(g0)
    c: Coincident(g3,g0)
    c: Weight(g1) = 1
    c: Equal(g1,g2)
    c: InternalAlignment(g1,g3)
    c: InternalAlignment(g2,g3)
    c: InternalAlignment(g4,g3)
    c: InternalAlignment(g5,g3)
    c: Block(g3)
    c: Coincident(g6,g0)
    c: Coincident(g6,g3)
    c: Horizontal(g6)
FEATURE [Part::Extrusion] Extrude019  label="caseScrewPillarBracket007"
  Base = -> Sketch025
  Dir = (0,0,1)
  DirMode = 2
  FaceMakerClass = Part::FaceMakerBullseye
  LengthFwd = 2.4
  LengthRev = 0
  Placement = pos=(101.3,29,65.23) rot=(0,1,0;1.5708rad)
  Solid = true
  Symmetric = false
FEATURE [Part::Box] Box011  label="frontCaseScrewPillarBracket"
  AttacherType = Attacher::AttachEngine3D
  Height = 2.4
  Length = 16
  Placement = pos=(87,28,2.3) rot=(0,0,1;0rad)
  Width = 7
FEATURE [Part::Box] Box012  label="frontCaseScrewPillarBracket001"
  AttacherType = Attacher::AttachEngine3D
  Height = 2.4
  Length = 16
  Placement = pos=(87,28,67.3) rot=(0,0,1;0rad)
  Width = 7
FEATURE [Sketcher::SketchObject] Sketch026
  FullyConstrained = true
  sketch-geometry (17):
    g0: Circle CenterX=-3.5 CenterY=23.5 CenterZ=0 NormalX=0 NormalY=0 NormalZ=1 AngleXU=0 Radius=1
    g1: Circle CenterX=-1 CenterY=15.25 CenterZ=0 NormalX=0 NormalY=0 NormalZ=1 AngleXU=0 Radius=1
    g2: Circle CenterX=-3.5 CenterY=7 CenterZ=0 NormalX=0 NormalY=0 NormalZ=1 AngleXU=0 Radius=1
    g3: BSplineCurve PolesCount=3 KnotsCount=2 Degree=2 IsPeriodic=0
    g4: GeomPoint X=-3.5 Y=23.5 Z=0
    g5: GeomPoint X=-3.5 Y=7 Z=0
    g6: Circle CenterX=-4.8 CenterY=30.5 CenterZ=0 NormalX=0 NormalY=0 NormalZ=1 AngleXU=0 Radius=1
    g7: Circle CenterX=-3.5 CenterY=30.5 CenterZ=0 NormalX=0 NormalY=0 NormalZ=1 AngleXU=0 Radius=1
    g8: Circle CenterX=-3.5 CenterY=29.2 CenterZ=0 NormalX=0 NormalY=0 NormalZ=1 AngleXU=0 Radius=1
    g9: BSplineCurve PolesCount=3 KnotsCount=2 Degree=2 IsPeriodic=0
    g10: GeomPoint X=-4.8 Y=30.5 Z=0
    g11: GeomPoint X=-3.5 Y=29.2 Z=0
    g12: LineSegment StartX=-3.5 StartY=29.2 StartZ=0 EndX=-3.5 EndY=23.5 EndZ=0
    g13: LineSegment StartX=-4.8 StartY=30.5 StartZ=0 EndX=0 EndY=30.5 EndZ=0
    g14: LineSegment StartX=-3.5 StartY=5 StartZ=0 EndX=-3.5 EndY=7 EndZ=0
    g15: LineSegment StartX=0 StartY=5 StartZ=0 EndX=0 EndY=30.5 EndZ=0
    g16: LineSegment StartX=-3.5 StartY=5 StartZ=0 EndX=0 EndY=5 EndZ=0
  constraints (33):
    c: Weight(g0) = 1
    c: Equal(g0,g1)
    c: Equal(g0,g2)
    c: InternalAlignment(g0,g3)
    c: InternalAlignment(g1,g3)
    c: InternalAlignment(g2,g3)
    c: InternalAlignment(g4,g3)
    c: InternalAlignment(g5,g3)
    c: Block(g3)
    c: Weight(g6) = 1
    c: Equal(g6,g7)
    c: Equal(g6,g8)
    c: InternalAlignment(g6,g9)
    c: InternalAlignment(g7,g9)
    c: InternalAlignment(g8,g9)
    c: InternalAlignment(g10,g9)
    c: InternalAlignment(g11,g9)
    c: Block(g9)
    c: Coincident(g12,g9)
    c: Coincident(g12,g3)
    c: Vertical(g12)
    c: Coincident(g13,g9)
    c: Horizontal(g13)
    c: Distance(g13) = 4.8
    c: Coincident(g14,g3)
    c: Vertical(g14)
    c: Coincident(g15,g13)
    c: Vertical(g15)
    c: Tangent(g15,g1)
    c: Distance(g14) = 2
    c: Coincident(g16,g14)
    c: Horizontal(g16)
    c: Coincident(g15,g16)
FEATURE [Part::Feature] Face050
  shape: bbox 4.8 x 25.5 x 2e-07 mm, 1 faces, 0 solids (baked)
FEATURE [Part::Revolution] Revolve054  label="moreFrontCaseScrewPost001"
  Angle = 360
  Axis = (0,1,0)
  Base = (0,0,0)
  FaceMakerClass = Part::FaceMakerBullseye
  Placement = pos=(102.5,4.5,3.5) rot=(0,0,1;0rad)
  Solid = false
  Source = -> Face050
  Symmetric = false
FEATURE [Part::Feature] Face051
  shape: bbox 4.8 x 25.5 x 2e-07 mm, 1 faces, 0 solids (baked)
FEATURE [Part::Revolution] Revolve055  label="moreFrontCaseScrewPost002"
  Angle = 360
  Axis = (0,1,0)
  Base = (0,0,0)
  FaceMakerClass = Part::FaceMakerBullseye
  Placement = pos=(102.5,4.5,68.5) rot=(0,0,1;0rad)
  Solid = false
  Source = -> Face051
  Symmetric = false
FEATURE [Sketcher::SketchObject] Sketch027
  FullyConstrained = true
  sketch-geometry (10):
    g0: LineSegment StartX=-1.6 StartY=4.7 StartZ=0 EndX=-1.6 EndY=1.7 EndZ=0
    g1: LineSegment StartX=-3.5 StartY=4.7 StartZ=0 EndX=-1.6 EndY=4.7 EndZ=0
    g2: LineSegment StartX=-1.6 StartY=1.7 StartZ=0 EndX=-1.6 EndY=1.5 EndZ=0
    g3: LineSegment StartX=-1.6 StartY=1.5 StartZ=0 EndX=-5.2 EndY=1.5 EndZ=0
    g4: Circle CenterX=-3.5 CenterY=4.7 CenterZ=0 NormalX=0 NormalY=0 NormalZ=1 AngleXU=0 Radius=1
    g5: Circle CenterX=-3.59627 CenterY=2.99743 CenterZ=0 NormalX=0 NormalY=0 NormalZ=1 AngleXU=0 Radius=1
    g6: Circle CenterX=-5.2 CenterY=1.5 CenterZ=0 NormalX=0 NormalY=0 NormalZ=1 AngleXU=0 Radius=1
    g7: BSplineCurve PolesCount=3 KnotsCount=2 Degree=2 IsPeriodic=0
    g8: GeomPoint X=-3.5 Y=4.7 Z=0
    g9: GeomPoint X=-5.2 Y=1.5 Z=0
  constraints (23):
    c: Vertical(g0)
    c: Distance(g0) = 3
    c: Coincident(g1,g0)
    c: Horizontal(g1)
    c: Block(g0)
    c: Block(g1)
    c: Coincident(g2,g0)
    c: Vertical(g2)
    c: Distance(g2) = 0.2
    c: Coincident(g3,g2)
    c: Horizontal(g3)
    c: Block(g3)
    c: Coincident(g7,g1)
    c: Weight(g4) = 1
    c: Equal(g4,g5)
    c: Equal(g4,g6)
    c: Coincident(g7,g3)
    c: InternalAlignment(g4,g7)
    c: InternalAlignment(g5,g7)
    c: InternalAlignment(g6,g7)
    c: InternalAlignment(g8,g7)
    c: InternalAlignment(g9,g7)
    c: Block(g7)
FEATURE [Sketcher::SketchObject] Sketch028
  FullyConstrained = true
  sketch-geometry (18):
    g0: LineSegment StartX=0 StartY=3e-16 StartZ=0 EndX=0 EndY=1.7 EndZ=0
    g1: LineSegment StartX=-3.5 StartY=0 StartZ=0 EndX=-3.5 EndY=0.9 EndZ=0
    g2: Circle CenterX=-2.7 CenterY=1.7 CenterZ=0 NormalX=0 NormalY=0 NormalZ=1 AngleXU=0 Radius=1
    g3: Circle CenterX=-3.5 CenterY=1.7 CenterZ=0 NormalX=0 NormalY=0 NormalZ=1 AngleXU=0 Radius=1
    g4: Circle CenterX=-3.5 CenterY=0.9 CenterZ=0 NormalX=0 NormalY=0 NormalZ=1 AngleXU=0 Radius=1
    g5: BSplineCurve PolesCount=3 KnotsCount=2 Degree=2 IsPeriodic=0
    g6: GeomPoint X=-2.7 Y=1.7 Z=0
    g7: GeomPoint X=-3.5 Y=0.9 Z=0
    g8: LineSegment StartX=-3.5 StartY=0 StartZ=0 EndX=-3.5 EndY=-7 EndZ=0
    g9: LineSegment StartX=0 StartY=3e-16 StartZ=0 EndX=0 EndY=-7 EndZ=0
    g10: LineSegment StartX=-3.5 StartY=-7 StartZ=0 EndX=0 EndY=-7 EndZ=0
    g11: LineSegment StartX=-2.7 StartY=1.7 StartZ=0 EndX=-1.6 EndY=1.7 EndZ=0
    g12: LineSegment StartX=0 StartY=1.7 StartZ=0 EndX=0 EndY=4.5 EndZ=0
    g13: LineSegment StartX=0 StartY=4.5 StartZ=0 EndX=0 EndY=10.8 EndZ=0
    g14: LineSegment StartX=0 StartY=10.8 StartZ=0 EndX=-2 EndY=10.8 EndZ=0
    g15: LineSegment StartX=-1.6 StartY=4.7 StartZ=0 EndX=-1.6 EndY=1.7 EndZ=0
    g16: LineSegment StartX=-1.6 StartY=4.7 StartZ=0 EndX=-2 EndY=4.7 EndZ=0
    g17: LineSegment StartX=-2 StartY=4.7 StartZ=0 EndX=-2 EndY=10.8 EndZ=0
  constraints (44):
    c: Vertical(g0)
    c: Vertical(g1)
    c: Distance(g1) = 0.9
    c: Block(g0)
    c: Distance(g0) = 1.7
    c: Weight(g2) = 1
    c: Equal(g2,g3)
    c: Equal(g2,g4)
    c: Coincident(g5,g1)
    c: InternalAlignment(g2,g5)
    c: InternalAlignment(g3,g5)
    c: InternalAlignment(g4,g5)
    c: InternalAlignment(g6,g5)
    c: InternalAlignment(g7,g5)
    c: Block(g5)
    c: Coincident(g8,g1)
    c: Vertical(g8)
    c: Distance(g8) = 7
    c: Vertical(g9)
    c: Equal(g8,g9) = 7
    c: Coincident(g9,g0)
    c: Coincident(g10,g8)
    c: Coincident(g10,g9)
    c: Horizontal(g10)
    c: Coincident(g11,g5)
    c: Horizontal(g11)
    c: Coincident(g12,g0)
    c: Vertical(g12)
    c: Distance(g12) = 2.8
    c: Coincident(g13,g12)
    c: Vertical(g13)
    c: Distance(g13) = 6.3
    c: Coincident(g14,g13)
    c: Horizontal(g14)
    c: Distance(g14) = 2
    c: Vertical(g15)
    c: Distance(g15) = 3
    c: Block(g11)
    c: Coincident(g15,g11)
    c: Coincident(g16,g15)
    c: Horizontal(g16)
    c: Coincident(g17,g16)
    c: Coincident(g17,g14)
    c: Vertical(g17)
FEATURE [Part::Revolution] Revolve040  label="backCaseScrewRetainer001"
  Angle = 360
  Axis = (0,1,0)
  Base = (0,0,0)
  FaceMakerClass = Part::FaceMakerBullseye
  Placement = pos=(12.5,3,10) rot=(0,0,1;0rad)
  Solid = false
  Source = -> Face036
  Symmetric = false
FEATURE [Part::Feature] Face055
  shape: bbox 3.5 x 30.2 x 2e-07 mm, 1 faces, 0 solids (baked)
FEATURE [Part::Revolution] Revolve059  label="backCaseScrewPost"
  Angle = 360
  Axis = (0,1,0)
  Base = (0,0,0)
  FaceMakerClass = Part::FaceMakerBullseye
  Placement = pos=(12.5,4.5,10) rot=(0,0,1;0rad)
  Solid = false
  Source = -> Face055
  Symmetric = false
FEATURE [Part::Feature] Face056
  shape: bbox 3.5 x 30.2 x 2e-07 mm, 1 faces, 0 solids (baked)
FEATURE [Part::Revolution] Revolve060  label="backCaseScrewPost001"
  Angle = 360
  Axis = (0,1,0)
  Base = (0,0,0)
  FaceMakerClass = Part::FaceMakerBullseye
  Placement = pos=(12.5,4.5,62) rot=(0,0,1;0rad)
  Solid = false
  Source = -> Face056
  Symmetric = false
FEATURE [Part::Feature] Face057
  shape: bbox 3.5 x 17.8 x 2e-07 mm, 1 faces, 0 solids (baked)
FEATURE [Part::Revolution] Revolve061  label="removeToCreateScrewAndThreadedInsertHole"
  Angle = 360
  Axis = (0,1,0)
  Base = (0,0,0)
  FaceMakerClass = Part::FaceMakerBullseye
  Placement = pos=(12.5,0,10) rot=(0,0,1;0rad)
  Solid = false
  Source = -> Face057
  Symmetric = false
FEATURE [Part::Feature] Face058
  shape: bbox 3.5 x 17.8 x 2e-07 mm, 1 faces, 0 solids (baked)
FEATURE [Part::Revolution] Revolve062  label="removeToCreateScrewAndThreadedInsertHole001"
  Angle = 360
  Axis = (0,1,0)
  Base = (0,0,0)
  FaceMakerClass = Part::FaceMakerBullseye
  Placement = pos=(12.5,0,62) rot=(0,0,1;0rad)
  Solid = false
  Source = -> Face058
  Symmetric = false
FEATURE [Part::Feature] Face059
  shape: bbox 3.5 x 17.8 x 2e-07 mm, 1 faces, 0 solids (baked)
FEATURE [Part::Revolution] Revolve063  label="removeToCreateScrewAndThreadedInsertHole002"
  Angle = 360
  Axis = (0,1,0)
  Base = (0,0,0)
  FaceMakerClass = Part::FaceMakerBullseye
  Placement = pos=(89.5,0,68.5) rot=(0,0,1;0rad)
  Solid = false
  Source = -> Face059
  Symmetric = false
FEATURE [Part::Feature] Face060
  shape: bbox 3.5 x 17.8 x 2e-07 mm, 1 faces, 0 solids (baked)
FEATURE [Part::Revolution] Revolve064  label="removeToCreateScrewAndThreadedInsertHole003"
  Angle = 360
  Axis = (0,1,0)
  Base = (0,0,0)
  FaceMakerClass = Part::FaceMakerBullseye
  Placement = pos=(89.5,0,3.5) rot=(0,0,1;0rad)
  Solid = false
  Source = -> Face060
  Symmetric = false
FEATURE [Part::Feature] Face061
  shape: bbox 3.5 x 17.8 x 2e-07 mm, 1 faces, 0 solids (baked)
FEATURE [Part::Revolution] Revolve065  label="removeToCreateScrewAndThreadedInsertHole004"
  Angle = 360
  Axis = (0,1,0)
  Base = (0,0,0)
  FaceMakerClass = Part::FaceMakerBullseye
  Placement = pos=(102.5,4.7,3.5) rot=(0,0,1;0rad)
  Solid = false
  Source = -> Face061
  Symmetric = false
FEATURE [Part::Feature] Face062
  shape: bbox 3.5 x 17.8 x 2e-07 mm, 1 faces, 0 solids (baked)
FEATURE [Part::Revolution] Revolve066  label="removeToCreateScrewAndThreadedInsertHole005"
  Angle = 360
  Axis = (0,1,0)
  Base = (0,0,0)
  FaceMakerClass = Part::FaceMakerBullseye
  Placement = pos=(102.5,4.7,68.5) rot=(0,0,1;0rad)
  Solid = false
  Source = -> Face062
  Symmetric = false
FEATURE [Part::MultiFuse] Fusion047  label="makeHoles"
  Shapes = -> [Revolve066,Revolve065,Revolve064,Revolve063,Revolve062,Revolve061]
FEATURE [Part::Feature] Face063
  shape: bbox 3.6 x 3.2 x 2e-07 mm, 1 faces, 0 solids (baked)
FEATURE [Part::Revolution] Revolve067  label="moreFrontCaseScrewRetainer002"
  Angle = 360
  Axis = (0,1,0)
  Base = (0,0,0)
  FaceMakerClass = Part::FaceMakerBullseye
  Placement = pos=(102.5,4.5,68.5) rot=(0,0,1;0rad)
  Solid = false
  Source = -> Face063
  Symmetric = false
FEATURE [Part::Feature] Face064
  shape: bbox 3.6 x 3.2 x 2e-07 mm, 1 faces, 0 solids (baked)
FEATURE [Part::Revolution] Revolve068  label="moreFrontCaseScrewRetainer003"
  Angle = 360
  Axis = (0,1,0)
  Base = (0,0,0)
  FaceMakerClass = Part::FaceMakerBullseye
  Placement = pos=(102.5,4.5,3.5) rot=(0,0,1;0rad)
  Solid = false
  Source = -> Face064
  Symmetric = false
FEATURE [Part::Cut] Cut014  label="bottom003"
  Base = -> Cut007
  Tool = -> Fusion047
FEATURE [Part::Feature] Face065
  shape: bbox 3.5 x 17.8 x 2e-07 mm, 1 faces, 0 solids (baked)
FEATURE [Part::Revolution] Revolve069  label="removeToCreateScrewAndThreadedInsertHole006"
  Angle = 360
  Axis = (0,1,0)
  Base = (0,0,0)
  FaceMakerClass = Part::FaceMakerBullseye
  Placement = pos=(12.5,0,10) rot=(0,0,1;0rad)
  Solid = false
  Source = -> Face065
  Symmetric = false
FEATURE [Part::Feature] Face066
  shape: bbox 3.5 x 17.8 x 2e-07 mm, 1 faces, 0 solids (baked)
FEATURE [Part::Revolution] Revolve070  label="removeToCreateScrewAndThreadedInsertHole007"
  Angle = 360
  Axis = (0,1,0)
  Base = (0,0,0)
  FaceMakerClass = Part::FaceMakerBullseye
  Placement = pos=(12.5,0,62) rot=(0,0,1;0rad)
  Solid = false
  Source = -> Face066
  Symmetric = false
FEATURE [Part::Feature] Face067
  shape: bbox 3.5 x 17.8 x 2e-07 mm, 1 faces, 0 solids (baked)
FEATURE [Part::Revolution] Revolve071  label="removeToCreateScrewAndThreadedInsertHole008"
  Angle = 360
  Axis = (0,1,0)
  Base = (0,0,0)
  FaceMakerClass = Part::FaceMakerBullseye
  Placement = pos=(89.5,0,68.5) rot=(0,0,1;0rad)
  Solid = false
  Source = -> Face067
  Symmetric = false
FEATURE [Part::Feature] Face068
  shape: bbox 3.5 x 17.8 x 2e-07 mm, 1 faces, 0 solids (baked)
FEATURE [Part::Revolution] Revolve072  label="removeToCreateScrewAndThreadedInsertHole009"
  Angle = 360
  Axis = (0,1,0)
  Base = (0,0,0)
  FaceMakerClass = Part::FaceMakerBullseye
  Placement = pos=(89.5,0,3.5) rot=(0,0,1;0rad)
  Solid = false
  Source = -> Face068
  Symmetric = false
FEATURE [Part::Feature] Face069
  shape: bbox 3.5 x 17.8 x 2e-07 mm, 1 faces, 0 solids (baked)
FEATURE [Part::Feature] Face070
  shape: bbox 3.5 x 17.8 x 2e-07 mm, 1 faces, 0 solids (baked)
FEATURE [Part::Revolution] Revolve073  label="removeToCreateScrewAndThreadedInsertHole010"
  Angle = 360
  Axis = (0,1,0)
  Base = (0,0,0)
  FaceMakerClass = Part::FaceMakerBullseye
  Placement = pos=(102.5,4.7,3.5) rot=(0,0,1;0rad)
  Solid = false
  Source = -> Face069
  Symmetric = false
FEATURE [Part::Revolution] Revolve074  label="removeToCreateScrewAndThreadedInsertHole011"
  Angle = 360
  Axis = (0,1,0)
  Base = (0,0,0)
  FaceMakerClass = Part::FaceMakerBullseye
  Placement = pos=(102.5,4.7,68.5) rot=(0,0,1;0rad)
  Solid = false
  Source = -> Face070
  Symmetric = false
FEATURE [Part::MultiFuse] Fusion048  label="makeHoles001"
  Shapes = -> [Revolve074,Revolve073,Revolve072,Revolve071,Revolve070,Revolve069]
FEATURE [Part::MultiFuse] Fusion049  label="caseScrewRetainers"
  Shapes = -> [Revolve067,Revolve068,Revolve048,Revolve047,Revolve039,Revolve040]
FEATURE [Part::Cut] Cut015  label="caseScrewRetainers001"
  Base = -> Fusion049
  Tool = -> Fusion048
FEATURE [Part::MultiFuse] Fusion050  label="casePillars"
  Shapes = -> [Revolve055,Revolve054,Revolve043,Revolve046,Revolve059,Revolve060]
FEATURE [Part::Feature] Face071 .. Face076  x6 (patterned run collapsed; names and placements below)
  shape: bbox 3.5 x 17.8 x 2e-07 mm, 1 faces, 0 solids (baked)
FEATURE [Part::Revolution] Revolve075  label="removeToCreateScrewAndThreadedInsertHole012"
  Angle = 360
  Axis = (0,1,0)
  Base = (0,0,0)
  FaceMakerClass = Part::FaceMakerBullseye
  Placement = pos=(12.5,0,10) rot=(0,0,1;0rad)
  Solid = false
  Source = -> Face071
  Symmetric = false
FEATURE [Part::Revolution] Revolve076  label="removeToCreateScrewAndThreadedInsertHole013"
  Angle = 360
  Axis = (0,1,0)
  Base = (0,0,0)
  FaceMakerClass = Part::FaceMakerBullseye
  Placement = pos=(12.5,0,62) rot=(0,0,1;0rad)
  Solid = false
  Source = -> Face072
  Symmetric = false
FEATURE [Part::Revolution] Revolve077  label="removeToCreateScrewAndThreadedInsertHole014"
  Angle = 360
  Axis = (0,1,0)
  Base = (0,0,0)
  FaceMakerClass = Part::FaceMakerBullseye
  Placement = pos=(89.5,0,68.5) rot=(0,0,1;0rad)
  Solid = false
  Source = -> Face073
  Symmetric = false
FEATURE [Part::Revolution] Revolve078  label="removeToCreateScrewAndThreadedInsertHole015"
  Angle = 360
  Axis = (0,1,0)
  Base = (0,0,0)
  FaceMakerClass = Part::FaceMakerBullseye
  Placement = pos=(89.5,0,3.5) rot=(0,0,1;0rad)
  Solid = false
  Source = -> Face074
  Symmetric = false
FEATURE [Part::Revolution] Revolve079  label="removeToCreateScrewAndThreadedInsertHole016"
  Angle = 360
  Axis = (0,1,0)
  Base = (0,0,0)
  FaceMakerClass = Part::FaceMakerBullseye
  Placement = pos=(102.5,4.7,3.5) rot=(0,0,1;0rad)
  Solid = false
  Source = -> Face075
  Symmetric = false
FEATURE [Part::Revolution] Revolve080  label="removeToCreateScrewAndThreadedInsertHole017"
  Angle = 360
  Axis = (0,1,0)
  Base = (0,0,0)
  FaceMakerClass = Part::FaceMakerBullseye
  Placement = pos=(102.5,4.7,68.5) rot=(0,0,1;0rad)
  Solid = false
  Source = -> Face076
  Symmetric = false
FEATURE [Part::MultiFuse] Fusion051  label="makeHoles002"
  Shapes = -> [Revolve080,Revolve079,Revolve078,Revolve077,Revolve076,Revolve075]
FEATURE [Part::Cut] Cut016  label="caesPillars"
  Base = -> Fusion050
  Tool = -> Fusion051
FEATURE [Part::Revolution] Revolve009  label="plugHousing016"
  Angle = 360
  Axis = (0,1,0)
  Base = (0,0,0)
  FaceMakerClass = Part::FaceMakerBullseye
  Placement = pos=(0,0,36.15) rot=(0,0,1;0rad)
  Solid = false
  Source = -> Face012
  Symmetric = false
FEATURE [Part::MultiFuse] Fusion014  label="plugHousing023"
  Placement = pos=(0,0,0) rot=(0,0,1;1.5708rad)
  Shapes = -> [Revolve011,Revolve009]
FEATURE [Part::Revolution] Revolve010  label="plugHousing017"
  Angle = 360
  Axis = (0,1,0)
  Base = (0,0,0)
  FaceMakerClass = Part::FaceMakerBullseye
  Placement = pos=(0,0,36.15) rot=(0,0,1;0rad)
  Solid = false
  Source = -> Face014
  Symmetric = false
FEATURE [Part::MultiFuse] Fusion015  label="plugHousing024"
  Placement = pos=(0,0,0) rot=(0,0,1;1.5708rad)
  Shapes = -> [Revolve010,Revolve015]
FEATURE [Part::Revolution] Revolve014  label="plugHousing026"
  Angle = 360
  Axis = (0,1,0)
  Base = (0,0,0)
  FaceMakerClass = Part::FaceMakerBullseye
  Placement = pos=(0,0,36.15) rot=(0,0,1;0rad)
  Solid = false
  Source = -> Face011
  Symmetric = false
FEATURE [Part::Revolution] Revolve013  label="plugHousing025"
  Angle = 360
  Axis = (0,1,0)
  Base = (0,0,0)
  FaceMakerClass = Part::FaceMakerBullseye
  Placement = pos=(0,0,36.15) rot=(0,0,1;0rad)
  Solid = false
  Source = -> Face015
  Symmetric = false
FEATURE [Part::MultiFuse] Fusion016  label="plugHousing028"
  Placement = pos=(0,19,0) rot=(0,0,1;3.14159rad)
  Shapes = -> [Fusion014,Fusion013]
FEATURE [Part::MultiFuse] Fusion011  label="plugHousing018"
  Placement = pos=(0,0,0) rot=(0,0,1;1.5708rad)
  Shapes = -> [Revolve014,Revolve013]
FEATURE [Part::MultiFuse] Fusion012  label="plugHousing019"
  Placement = pos=(0,19,0) rot=(0,0,1;3.14159rad)
  Shapes = -> [Fusion011,Fusion015]
FEATURE [Part::MultiFuse] Fusion017  label="plugHousing029"
  Placement = pos=(122.621,0,-0.15) rot=(0,0,1;0rad)
  Shapes = -> [Fusion016,Fusion012]
FEATURE [Part::MultiFuse] Fusion052  label="casePillarRetainers"
  Shapes = -> [Extrude012,Extrude013,Extrude014,Extrude015,Extrude016,Extrude017,Extrude018,Extrude019,Box011,Box012]
FEATURE [Part::Feature] Face077
  shape: bbox 3.5 x 17.8 x 2e-07 mm, 1 faces, 0 solids (baked)
FEATURE [Part::Revolution] Revolve081  label="removeToCreateScrewAndThreadedInsertHole018"
  Angle = 360
  Axis = (0,1,0)
  Base = (0,0,0)
  FaceMakerClass = Part::FaceMakerBullseye
  Placement = pos=(62.3,30.3,19.7) rot=(0,0,1;0rad)
  Solid = false
  Source = -> Face077
  Symmetric = false
FEATURE [Part::Feature] Face078
  shape: bbox 3.5 x 17.8 x 2e-07 mm, 1 faces, 0 solids (baked)
FEATURE [Part::Revolution] Revolve082  label="removeToCreateScrewAndThreadedInsertHole019"
  Angle = 360
  Axis = (0,1,0)
  Base = (0,0,0)
  FaceMakerClass = Part::FaceMakerBullseye
  Placement = pos=(62.3,30.3,51.7) rot=(0,0,1;0rad)
  Solid = false
  Source = -> Face078
  Symmetric = false
FEATURE [Part::Feature] Face079
  shape: bbox 3.5 x 17.8 x 2e-07 mm, 1 faces, 0 solids (baked)
FEATURE [Part::Revolution] Revolve083  label="removeToCreateScrewAndThreadedInsertHole020"
  Angle = 360
  Axis = (0,1,0)
  Base = (0,0,0)
  FaceMakerClass = Part::FaceMakerBullseye
  Placement = pos=(30.3,30.3,19.7) rot=(0,0,1;0rad)
  Solid = false
  Source = -> Face079
  Symmetric = false
FEATURE [Part::Feature] Face080
  shape: bbox 3.5 x 17.8 x 2e-07 mm, 1 faces, 0 solids (baked)
FEATURE [Part::Revolution] Revolve084  label="removeToCreateScrewAndThreadedInsertHole021"
  Angle = 360
  Axis = (0,1,0)
  Base = (0,0,0)
  FaceMakerClass = Part::FaceMakerBullseye
  Placement = pos=(30.3,30.3,51.7) rot=(0,0,1;0rad)
  Solid = false
  Source = -> Face080
  Symmetric = false
FEATURE [Part::MultiFuse] Fusion053  label="createThreadedInsertHolesForFan"
  Shapes = -> [Revolve081,Revolve082,Revolve083,Revolve084]
FEATURE [Part::Cut] Cut017  label="fanScrewHousing001"
  Base = -> Fusion046
  Tool = -> Fusion053
FEATURE [Part::Feature] Face081
  shape: bbox 3.5 x 17.8 x 2e-07 mm, 1 faces, 0 solids (baked)
FEATURE [Part::Revolution] Revolve085  label="removeToCreateScrewAndThreadedInsertHole022"
  Angle = 360
  Axis = (0,1,0)
  Base = (0,0,0)
  FaceMakerClass = Part::FaceMakerBullseye
  Placement = pos=(62.3,30.3,19.7) rot=(0,0,1;0rad)
  Solid = false
  Source = -> Face081
  Symmetric = false
FEATURE [Part::Feature] Face082
  shape: bbox 3.5 x 17.8 x 2e-07 mm, 1 faces, 0 solids (baked)
FEATURE [Part::Revolution] Revolve086  label="removeToCreateScrewAndThreadedInsertHole023"
  Angle = 360
  Axis = (0,1,0)
  Base = (0,0,0)
  FaceMakerClass = Part::FaceMakerBullseye
  Placement = pos=(62.3,30.3,51.7) rot=(0,0,1;0rad)
  Solid = false
  Source = -> Face082
  Symmetric = false
FEATURE [Part::Feature] Face083
  shape: bbox 3.5 x 17.8 x 2e-07 mm, 1 faces, 0 solids (baked)
FEATURE [Part::Revolution] Revolve087  label="removeToCreateScrewAndThreadedInsertHole024"
  Angle = 360
  Axis = (0,1,0)
  Base = (0,0,0)
  FaceMakerClass = Part::FaceMakerBullseye
  Placement = pos=(30.3,30.3,19.7) rot=(0,0,1;0rad)
  Solid = false
  Source = -> Face083
  Symmetric = false
FEATURE [Part::Feature] Face084
  shape: bbox 3.5 x 17.8 x 2e-07 mm, 1 faces, 0 solids (baked)
FEATURE [Part::Revolution] Revolve088  label="removeToCreateScrewAndThreadedInsertHole025"
  Angle = 360
  Axis = (0,1,0)
  Base = (0,0,0)
  FaceMakerClass = Part::FaceMakerBullseye
  Placement = pos=(30.3,30.3,51.7) rot=(0,0,1;0rad)
  Solid = false
  Source = -> Face084
  Symmetric = false
FEATURE [Part::MultiFuse] Fusion054  label="createThreadedInsertHolesForFan001"
  Shapes = -> [Revolve085,Revolve086,Revolve087,Revolve088]
FEATURE [Part::Cut] Cut018  label="top007"
  Base = -> Fusion040
  Tool = -> Fusion054
FEATURE [Sketcher::SketchObject] Sketch029
  FullyConstrained = false
  Placement = pos=(0,0,0) rot=(1,0,0;1.5708rad)
  sketch-geometry (24):
    g0: ArcOfCircle CenterX=-4 CenterY=-10.5 CenterZ=0 NormalX=0 NormalY=0 NormalZ=1 AngleXU=0 Radius=1.5 StartAngle=6e-16 EndAngle=3.14159
    g1: ArcOfCircle CenterX=-34.2 CenterY=-10.5 CenterZ=0 NormalX=0 NormalY=0 NormalZ=1 AngleXU=0 Radius=1.5 StartAngle=0 EndAngle=3.14159
    g2: ArcOfCircle CenterX=-34.2 CenterY=-27.7 CenterZ=0 NormalX=0 NormalY=0 NormalZ=1 AngleXU=0 Radius=1.5 StartAngle=3.14159 EndAngle=6.28319
    g3: ArcOfCircle CenterX=-4 CenterY=-27.7 CenterZ=0 NormalX=0 NormalY=0 NormalZ=1 AngleXU=0 Radius=1.5 StartAngle=3.1416 EndAngle=6.28319
    g4: ArcOfCircle CenterX=-10 CenterY=-4.3 CenterZ=0 NormalX=0 NormalY=0 NormalZ=1 AngleXU=0 Radius=1.5 StartAngle=2e-16 EndAngle=3.14159
    g5: ArcOfCircle CenterX=-16.1 CenterY=-1.8 CenterZ=0 NormalX=0 NormalY=0 NormalZ=1 AngleXU=0 Radius=1.5 StartAngle=5e-16 EndAngle=3.14159
    g6: ArcOfCircle CenterX=-22.1 CenterY=-1.8 CenterZ=0 NormalX=0 NormalY=0 NormalZ=1 AngleXU=0 Radius=1.5 StartAngle=5e-16 EndAngle=3.14159
    g7: ArcOfCircle CenterX=-28.2 CenterY=-4.3 CenterZ=0 NormalX=0 NormalY=0 NormalZ=1 AngleXU=0 Radius=1.5 StartAngle=2e-16 EndAngle=3.14159
    g8: ArcOfCircle CenterX=-10 CenterY=-33.9 CenterZ=0 NormalX=0 NormalY=0 NormalZ=1 AngleXU=0 Radius=1.5 StartAngle=3.14159 EndAngle=6.28319
    g9: ArcOfCircle CenterX=-16.1 CenterY=-36.4 CenterZ=0 NormalX=0 NormalY=0 NormalZ=1 AngleXU=0 Radius=1.5 StartAngle=3.14159 EndAngle=6.28319
    g10: ArcOfCircle CenterX=-22.1 CenterY=-36.4 CenterZ=0 NormalX=0 NormalY=0 NormalZ=1 AngleXU=0 Radius=1.5 StartAngle=3.14159 EndAngle=6.28319
    g11: ArcOfCircle CenterX=-28.2 CenterY=-33.9 CenterZ=0 NormalX=0 NormalY=0 NormalZ=1 AngleXU=0 Radius=1.5 StartAngle=3.14159 EndAngle=6.28319
    g12: LineSegment StartX=-35.7 StartY=-10.5 StartZ=0 EndX=-35.7 EndY=-27.7 EndZ=0
    g13: LineSegment StartX=-32.7 StartY=-10.5 StartZ=0 EndX=-32.7 EndY=-27.7 EndZ=0
    g14: LineSegment StartX=-29.7 StartY=-33.9 StartZ=0 EndX=-29.7 EndY=-4.3 EndZ=0
    g15: LineSegment StartX=-26.7 StartY=-33.9 StartZ=0 EndX=-26.7 EndY=-4.3 EndZ=0
    g16: LineSegment StartX=-2.5 StartY=-10.5 StartZ=0 EndX=-2.5 EndY=-27.7 EndZ=0
    g17: LineSegment StartX=-8.5 StartY=-4.3 StartZ=0 EndX=-8.5 EndY=-33.9 EndZ=0
    g18: LineSegment StartX=-5.5 StartY=-10.5 StartZ=0 EndX=-5.5 EndY=-27.7 EndZ=0
    g19: LineSegment StartX=-11.5 StartY=-4.3 StartZ=0 EndX=-11.5 EndY=-33.9 EndZ=0
    g20: LineSegment StartX=-14.6 StartY=-1.8 StartZ=0 EndX=-14.6 EndY=-36.4 EndZ=0
    g21: LineSegment StartX=-17.6 StartY=-1.8 StartZ=0 EndX=-17.6 EndY=-36.4 EndZ=0
    g22: LineSegment StartX=-20.6 StartY=-36.4 StartZ=0 EndX=-20.6 EndY=-1.8 EndZ=0
    g23: LineSegment StartX=-23.6 StartY=-1.8 StartZ=0 EndX=-23.6 EndY=-36.4 EndZ=0
  constraints (48):
    c: Block(g0)
    c: Block(g1)
    c: Block(g2)
    c: Block(g3)
    c: Block(g4)
    c: Block(g5)
    c: Block(g6)
    c: Block(g7)
    c: Block(g8)
    c: Block(g9)
    c: Block(g10)
    c: Block(g11)
    c: Coincident(g12,g1)
    c: Coincident(g12,g2)
    c: Vertical(g12)
    c: Coincident(g13,g1)
    c: Coincident(g13,g2)
    c: Vertical(g13)
    c: Coincident(g14,g11)
    c: Coincident(g14,g7)
    c: Vertical(g14)
    c: Coincident(g15,g11)
    c: Coincident(g15,g7)
    c: Vertical(g15)
    c: Coincident(g16,g0)
    c: Coincident(g16,g3)
    c: Vertical(g16)
    c: Coincident(g17,g4)
    c: Coincident(g17,g8)
    c: Vertical(g17)
    c: Coincident(g18,g0)
    c: Coincident(g18,g3)
    c: Vertical(g18)
    c: Coincident(g19,g4)
    c: Coincident(g19,g8)
    c: Vertical(g19)
    c: Coincident(g20,g5)
    c: Coincident(g20,g9)
    c: Vertical(g20)
    c: Coincident(g21,g5)
    c: Coincident(g21,g9)
    c: Vertical(g21)
    c: Coincident(g22,g10)
    c: Coincident(g22,g6)
    c: Vertical(g22)
    c: Coincident(g23,g6)
    c: Coincident(g23,g10)
    c: Vertical(g23)
FEATURE [Part::Extrusion] Extrude020  label="removeToCreateFanGrillHoles"
  Base = -> Sketch029
  Dir = (0,-1,6e-16)
  DirMode = 2
  FaceMakerClass = Part::FaceMakerBullseye
  LengthFwd = 10
  LengthRev = 0
  Placement = pos=(65.4,44,54.82) rot=(0,0,1;0rad)
  Solid = true
  Symmetric = false
FEATURE [Part::MultiFuse] Fusion055  label="top008"
  Shapes = -> [Cut017,Cut018]
FEATURE [Part::Cut] Cut019  label="top009"
  Base = -> Fusion055
  Tool = -> Extrude020
FEATURE [App::MeasureDistance] Distance003  label="Distance: 71.95 mm"
  Distance = 71.9513
  P1 = (117,38,72)
  P2 = (117,38,0.0487319)
FEATURE [Sketcher::SketchObject] Sketch030
  FullyConstrained = true
  Placement = pos=(117,19,0) rot=(0.57735,0.57735,0.57735;2.0944rad)
  sketch-geometry (48):
    g0: LineSegment StartX=-49.19 StartY=69.25 StartZ=0 EndX=-49.19 EndY=66.25 EndZ=0
    g1: LineSegment StartX=-49.19 StartY=63.5 StartZ=0 EndX=-49.19 EndY=60.5 EndZ=0
    g2: LineSegment StartX=-49.19 StartY=57.75 StartZ=0 EndX=-49.19 EndY=54.75 EndZ=0
    g3: LineSegment StartX=-49.19 StartY=52 StartZ=0 EndX=-49.19 EndY=49 EndZ=0
    g4: LineSegment StartX=-49.19 StartY=46.25 StartZ=0 EndX=-49.19 EndY=43.25 EndZ=0
    g5: LineSegment StartX=-49.19 StartY=40.5 StartZ=0 EndX=-49.19 EndY=37.5 EndZ=0
    g6: LineSegment StartX=-49.19 StartY=34.5 StartZ=0 EndX=-49.19 EndY=31.5 EndZ=0
    g7: LineSegment StartX=-49.19 StartY=28.75 StartZ=0 EndX=-49.19 EndY=25.75 EndZ=0
    g8: LineSegment StartX=-49.19 StartY=23 StartZ=0 EndX=-49.19 EndY=20 EndZ=0
    g9: LineSegment StartX=-49.19 StartY=17.25 StartZ=0 EndX=-49.19 EndY=14.25 EndZ=0
    g10: LineSegment StartX=-49.19 StartY=11.5 StartZ=0 EndX=-49.19 EndY=8.5 EndZ=0
    g11: LineSegment StartX=-49.19 StartY=5.75 StartZ=0 EndX=-49.19 EndY=2.75 EndZ=0
    g12: ArcOfCircle CenterX=-1.5 CenterY=67.75 CenterZ=0 NormalX=0 NormalY=0 NormalZ=1 AngleXU=0 Radius=1.5 StartAngle=4.71239 EndAngle=7.85398
    g13: ArcOfCircle CenterX=-1.5 CenterY=62 CenterZ=0 NormalX=0 NormalY=0 NormalZ=1 AngleXU=0 Radius=1.5 StartAngle=4.71239 EndAngle=7.85398
    g14: ArcOfCircle CenterX=-1.5 CenterY=56.25 CenterZ=0 NormalX=0 NormalY=0 NormalZ=1 AngleXU=0 Radius=1.5 StartAngle=4.71239 EndAngle=7.85398
    g15: ArcOfCircle CenterX=-11.49 CenterY=50.5 CenterZ=0 NormalX=0 NormalY=0 NormalZ=1 AngleXU=0 Radius=1.5 StartAngle=4.71239 EndAngle=7.85398
    g16: ArcOfCircle CenterX=-16.28 CenterY=44.75 CenterZ=0 NormalX=0 NormalY=0 NormalZ=1 AngleXU=0 Radius=1.5 StartAngle=4.71239 EndAngle=7.85398
    g17: ArcOfCircle CenterX=-18.2337 CenterY=39 CenterZ=0 NormalX=0 NormalY=0 NormalZ=1 AngleXU=0 Radius=1.5 StartAngle=4.71485 EndAngle=7.85398
    g18: ArcOfCircle CenterX=-16.2837 CenterY=27.25 CenterZ=0 NormalX=0 NormalY=0 NormalZ=1 AngleXU=0 Radius=1.5 StartAngle=4.71485 EndAngle=7.85398
    g19: ArcOfCircle CenterX=-18.2337 CenterY=33 CenterZ=0 NormalX=0 NormalY=0 NormalZ=1 AngleXU=0 Radius=1.5 StartAngle=4.71485 EndAngle=7.85398
    g20: ArcOfCircle CenterX=-11.49 CenterY=21.5 CenterZ=0 NormalX=0 NormalY=0 NormalZ=1 AngleXU=0 Radius=1.5 StartAngle=4.71239 EndAngle=7.85398
    g21: ArcOfCircle CenterX=-1.5 CenterY=4.25 CenterZ=0 NormalX=0 NormalY=0 NormalZ=1 AngleXU=0 Radius=1.5 StartAngle=4.71239 EndAngle=7.85398
    g22: ArcOfCircle CenterX=-1.5 CenterY=10 CenterZ=0 NormalX=0 NormalY=0 NormalZ=1 AngleXU=0 Radius=1.5 StartAngle=4.71239 EndAngle=7.85398
    g23: ArcOfCircle CenterX=-1.5 CenterY=15.75 CenterZ=0 NormalX=0 NormalY=0 NormalZ=1 AngleXU=0 Radius=1.5 StartAngle=4.71239 EndAngle=7.85398
    g24: LineSegment StartX=-49.19 StartY=69.25 StartZ=0 EndX=-1.5 EndY=69.25 EndZ=0
    g25: LineSegment StartX=-49.19 StartY=66.25 StartZ=0 EndX=-1.5 EndY=66.25 EndZ=0
    g26: LineSegment StartX=-49.19 StartY=63.5 StartZ=0 EndX=-1.5 EndY=63.5 EndZ=0
    g27: LineSegment StartX=-49.19 StartY=60.5 StartZ=0 EndX=-1.5 EndY=60.5 EndZ=0
    g28: LineSegment StartX=-49.19 StartY=57.75 StartZ=0 EndX=-1.5 EndY=57.75 EndZ=0
    g29: LineSegment StartX=-49.19 StartY=54.75 StartZ=0 EndX=-1.5 EndY=54.75 EndZ=0
    g30: LineSegment StartX=-49.19 StartY=52 StartZ=0 EndX=-11.49 EndY=52 EndZ=0
    g31: LineSegment StartX=-49.19 StartY=49 StartZ=0 EndX=-11.49 EndY=49 EndZ=0
    g32: LineSegment StartX=-49.19 StartY=46.25 StartZ=0 EndX=-16.28 EndY=46.25 EndZ=0
    g33: LineSegment StartX=-49.19 StartY=43.25 StartZ=0 EndX=-16.28 EndY=43.25 EndZ=0
    g34: LineSegment StartX=-49.19 StartY=40.5 StartZ=0 EndX=-18.2337 EndY=40.5 EndZ=0
    g35: LineSegment StartX=-49.19 StartY=37.5 StartZ=0 EndX=-18.23 EndY=37.5 EndZ=0
    g36: LineSegment StartX=-49.19 StartY=34.5 StartZ=0 EndX=-18.2337 EndY=34.5 EndZ=0
    g37: LineSegment StartX=-49.19 StartY=31.5 StartZ=0 EndX=-18.23 EndY=31.5 EndZ=0
    g38: LineSegment StartX=-49.19 StartY=28.75 StartZ=0 EndX=-16.2837 EndY=28.75 EndZ=0
    g39: LineSegment StartX=-49.19 StartY=25.75 StartZ=0 EndX=-16.28 EndY=25.75 EndZ=0
    g40: LineSegment StartX=-49.19 StartY=23 StartZ=0 EndX=-11.49 EndY=23 EndZ=0
    g41: LineSegment StartX=-49.19 StartY=20 StartZ=0 EndX=-11.49 EndY=20 EndZ=0
    g42: LineSegment StartX=-49.19 StartY=17.25 StartZ=0 EndX=-1.5 EndY=17.25 EndZ=0
    g43: LineSegment StartX=-49.19 StartY=14.25 StartZ=0 EndX=-1.5 EndY=14.25 EndZ=0
    g44: LineSegment StartX=-49.19 StartY=11.5 StartZ=0 EndX=-1.5 EndY=11.5 EndZ=0
    g45: LineSegment StartX=-49.19 StartY=8.5 StartZ=0 EndX=-1.5 EndY=8.5 EndZ=0
    g46: LineSegment StartX=-49.19 StartY=5.75 StartZ=0 EndX=-1.5 EndY=5.75 EndZ=0
    g47: LineSegment StartX=-49.19 StartY=2.75 StartZ=0 EndX=-1.5 EndY=2.75 EndZ=0
  constraints (120):
    c: Vertical(g0)
    c: Distance(g0) = 3
    c: Block(g0)
    c: Vertical(g1)
    c: Distance(g1) = 3
    c: Vertical(g2)
    c: Equal(g0,g2) = 3
    c: Block(g2)
    c: Vertical(g3)
    c: Equal(g1,g3) = 3
    c: Vertical(g4)
    c: Equal(g0,g4) = 3
    c: Block(g4)
    c: Vertical(g5)
    c: Equal(g1,g5) = 3
    c: Vertical(g6)
    c: Equal(g0,g6) = 3
    c: Block(g6)
    c: Vertical(g7)
    c: Equal(g1,g7) = 3
    c: Vertical(g8)
    c: Equal(g0,g8) = 3
    c: Block(g8)
    c: Vertical(g9)
    c: Equal(g1,g9) = 3
    c: Vertical(g10)
    c: Equal(g0,g10) = 3
    c: Block(g10)
    c: Vertical(g11)
    c: Equal(g1,g11) = 3
    c: Block(g12)
    c: Block(g13)
    c: Block(g14)
    c: Block(g15)
    c: Block(g16)
    c: Block(g17)
    c: Block(g18)
    c: Block(g19)
    c: Block(g20)
    c: Block(g21)
    c: Block(g22)
    c: Block(g23)
    c: Block(g11)
    c: Block(g9)
    c: Block(g7)
    c: Block(g5)
    c: Block(g3)
    c: Block(g1)
    c: Coincident(g24,g0)
    c: Coincident(g24,g12)
    c: Horizontal(g24)
    c: Coincident(g25,g0)
    c: Coincident(g25,g12)
    c: Horizontal(g25)
    c: Coincident(g26,g1)
    c: Coincident(g26,g13)
    c: Horizontal(g26)
    c: Coincident(g27,g1)
    c: Coincident(g27,g13)
    c: Horizontal(g27)
    c: Coincident(g28,g2)
    c: Coincident(g28,g14)
    c: Horizontal(g28)
    c: Coincident(g29,g2)
    c: Coincident(g29,g14)
    c: Horizontal(g29)
    c: Coincident(g30,g3)
    c: Coincident(g30,g15)
    c: Horizontal(g30)
    c: Coincident(g31,g3)
    c: Coincident(g31,g15)
    c: Horizontal(g31)
    c: Coincident(g32,g4)
    c: Coincident(g32,g16)
    c: Horizontal(g32)
    c: Coincident(g33,g4)
    c: Coincident(g33,g16)
    c: Horizontal(g33)
    c: Coincident(g34,g5)
    c: Coincident(g34,g17)
    c: Horizontal(g34)
    c: Coincident(g35,g5)
    c: Coincident(g35,g17)
    c: Horizontal(g35)
    c: Coincident(g36,g6)
    c: Coincident(g36,g19)
    c: Horizontal(g36)
    c: Coincident(g37,g6)
    c: Coincident(g37,g19)
    c: Horizontal(g37)
    c: Coincident(g38,g7)
    c: Coincident(g38,g18)
    c: Horizontal(g38)
    c: Coincident(g39,g7)
    c: Coincident(g39,g18)
    c: Horizontal(g39)
    c: Coincident(g40,g8)
    c: Coincident(g40,g20)
    c: Horizontal(g40)
    c: Coincident(g41,g8)
    c: Coincident(g41,g20)
    c: Horizontal(g41)
    c: Coincident(g42,g9)
    c: Coincident(g42,g23)
    c: Horizontal(g42)
    c: Coincident(g43,g9)
    c: Coincident(g43,g23)
    c: Horizontal(g43)
    c: Coincident(g44,g10)
    c: Coincident(g44,g22)
    c: Horizontal(g44)
    c: Coincident(g45,g10)
    c: Coincident(g45,g22)
    c: Horizontal(g45)
    c: Coincident(g46,g11)
    c: Coincident(g46,g21)
    c: Horizontal(g46)
    c: Coincident(g47,g11)
    c: Coincident(g47,g21)
    c: Horizontal(g47)
FEATURE [Sketcher::SketchObject] Sketch031
  FullyConstrained = true
  Placement = pos=(117,19,0) rot=(0.57735,0.57735,0.57735;2.0944rad)
  sketch-geometry (24):
    g0: ArcOfCircle CenterX=-49.19 CenterY=67.75 CenterZ=0 NormalX=0 NormalY=0 NormalZ=1 AngleXU=0 Radius=1.5 StartAngle=1.5708 EndAngle=4.71239
    g1: ArcOfCircle CenterX=-49.19 CenterY=62 CenterZ=0 NormalX=0 NormalY=0 NormalZ=1 AngleXU=0 Radius=1.5 StartAngle=1.5708 EndAngle=4.71239
    g2: ArcOfCircle CenterX=-49.19 CenterY=56.25 CenterZ=0 NormalX=0 NormalY=0 NormalZ=1 AngleXU=0 Radius=1.5 StartAngle=1.5708 EndAngle=4.71239
    g3: ArcOfCircle CenterX=-49.19 CenterY=50.5 CenterZ=0 NormalX=0 NormalY=0 NormalZ=1 AngleXU=0 Radius=1.5 StartAngle=1.5708 EndAngle=4.71239
    g4: ArcOfCircle CenterX=-49.19 CenterY=44.75 CenterZ=0 NormalX=0 NormalY=0 NormalZ=1 AngleXU=0 Radius=1.5 StartAngle=1.5708 EndAngle=4.71239
    g5: ArcOfCircle CenterX=-49.19 CenterY=39 CenterZ=0 NormalX=0 NormalY=0 NormalZ=1 AngleXU=0 Radius=1.5 StartAngle=1.5708 EndAngle=4.71239
    g6: ArcOfCircle CenterX=-49.19 CenterY=33 CenterZ=0 NormalX=0 NormalY=0 NormalZ=1 AngleXU=0 Radius=1.5 StartAngle=1.5708 EndAngle=4.71239
    g7: ArcOfCircle CenterX=-49.19 CenterY=27.25 CenterZ=0 NormalX=0 NormalY=0 NormalZ=1 AngleXU=0 Radius=1.5 StartAngle=1.5708 EndAngle=4.71239
    g8: ArcOfCircle CenterX=-49.19 CenterY=21.5 CenterZ=0 NormalX=0 NormalY=0 NormalZ=1 AngleXU=0 Radius=1.5 StartAngle=1.5708 EndAngle=4.71239
    g9: ArcOfCircle CenterX=-49.19 CenterY=15.75 CenterZ=0 NormalX=0 NormalY=0 NormalZ=1 AngleXU=0 Radius=1.5 StartAngle=1.5708 EndAngle=4.71239
    g10: ArcOfCircle CenterX=-49.19 CenterY=10 CenterZ=0 NormalX=0 NormalY=0 NormalZ=1 AngleXU=0 Radius=1.5 StartAngle=1.5708 EndAngle=4.71239
    g11: ArcOfCircle CenterX=-49.19 CenterY=4.25 CenterZ=0 NormalX=0 NormalY=0 NormalZ=1 AngleXU=0 Radius=1.5 StartAngle=1.5708 EndAngle=4.71239
    g12: LineSegment StartX=-49.19 StartY=69.25 StartZ=0 EndX=-49.19 EndY=66.25 EndZ=0
    g13: LineSegment StartX=-49.19 StartY=63.5 StartZ=0 EndX=-49.19 EndY=60.5 EndZ=0
    g14: LineSegment StartX=-49.19 StartY=57.75 StartZ=0 EndX=-49.19 EndY=54.75 EndZ=0
    g15: LineSegment StartX=-49.19 StartY=52 StartZ=0 EndX=-49.19 EndY=49 EndZ=0
    g16: LineSegment StartX=-49.19 StartY=46.25 StartZ=0 EndX=-49.19 EndY=43.25 EndZ=0
    g17: LineSegment StartX=-49.19 StartY=40.5 StartZ=0 EndX=-49.19 EndY=37.5 EndZ=0
    g18: LineSegment StartX=-49.19 StartY=34.5 StartZ=0 EndX=-49.19 EndY=31.5 EndZ=0
    g19: LineSegment StartX=-49.19 StartY=28.75 StartZ=0 EndX=-49.19 EndY=25.75 EndZ=0
    g20: LineSegment StartX=-49.19 StartY=23 StartZ=0 EndX=-49.19 EndY=20 EndZ=0
    g21: LineSegment StartX=-49.19 StartY=17.25 StartZ=0 EndX=-49.19 EndY=14.25 EndZ=0
    g22: LineSegment StartX=-49.19 StartY=11.5 StartZ=0 EndX=-49.19 EndY=8.5 EndZ=0
    g23: LineSegment StartX=-49.19 StartY=5.75 StartZ=0 EndX=-49.19 EndY=2.75 EndZ=0
  constraints (48):
    c: Block(g0)
    c: Block(g1)
    c: Block(g2)
    c: Block(g3)
    c: Block(g4)
    c: Block(g5)
    c: Block(g6)
    c: Block(g7)
    c: Block(g8)
    c: Block(g9)
    c: Block(g10)
    c: Block(g11)
    c: Coincident(g12,g0)
    c: Coincident(g12,g0)
    c: Vertical(g12)
    c: Vertical(g13)
    c: Coincident(g13,g1)
    c: Vertical(g14)
    c: Coincident(g14,g2)
    c: Vertical(g15)
    c: Coincident(g15,g3)
    c: Vertical(g16)
    c: Coincident(g16,g4)
    c: Vertical(g17)
    c: Coincident(g17,g5)
    c: Vertical(g18)
    c: Coincident(g18,g6)
    c: Vertical(g19)
    c: Coincident(g19,g7)
    c: Vertical(g20)
    c: Coincident(g20,g8)
    c: Vertical(g21)
    c: Coincident(g21,g9)
    c: Vertical(g22)
    c: Coincident(g22,g10)
    c: Vertical(g23)
    c: Coincident(g23,g11)
    c: Block(g23)
    c: Block(g22)
    c: Block(g21)
    c: Block(g20)
    c: Block(g13)
    c: Block(g14)
    c: Block(g15)
    c: Block(g16)
    c: Block(g17)
    c: Block(g18)
    c: Block(g19)
FEATURE [Part::Extrusion] Extrude021
  Base = -> Sketch031
  Dir = (1,0,0)
  DirMode = 2
  FaceMakerClass = Part::FaceMakerBullseye
  LengthFwd = 20
  LengthRev = 0
  Placement = pos=(117,136,0) rot=(0,0,1;-1.5708rad)
  Solid = true
  Symmetric = false
FEATURE [Part::Extrusion] Extrude022
  Base = -> Sketch030
  Dir = (1,-2e-16,2e-16)
  DirMode = 2
  FaceMakerClass = Part::FaceMakerBullseye
  LengthFwd = 19
  LengthRev = 0
  Placement = pos=(-19,0,0) rot=(0,0,1;0rad)
  Solid = true
  Symmetric = false
